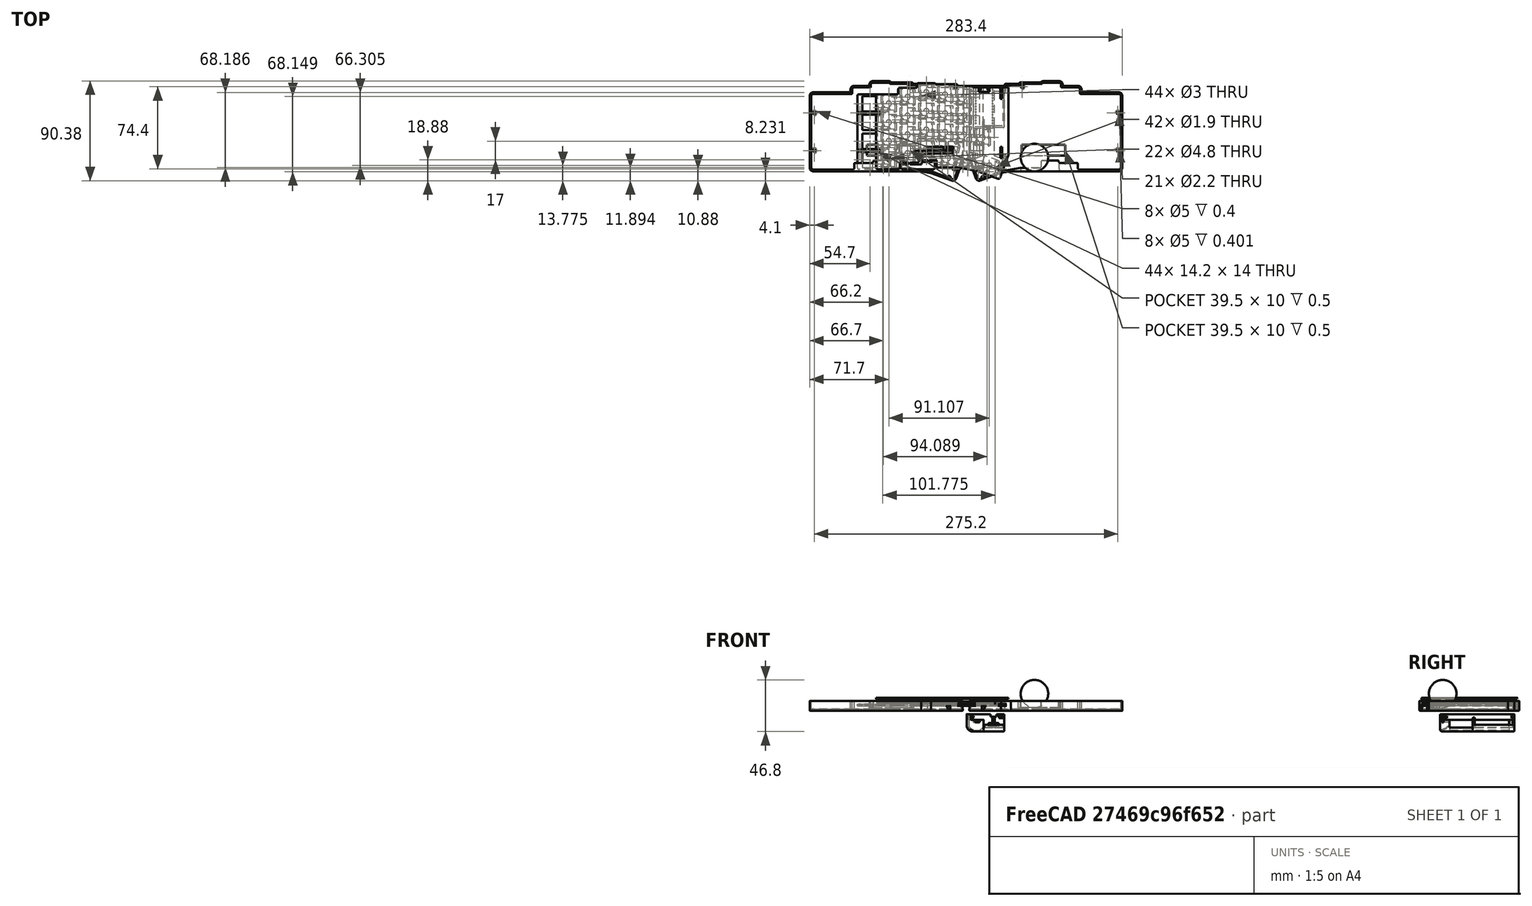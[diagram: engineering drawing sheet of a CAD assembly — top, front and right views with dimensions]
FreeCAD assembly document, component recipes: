
FREECAD ASSEMBLY — COMPONENT RECIPES ("simple-case-MS")

This assembly document has 5 components, labeled P0..P4 below (a component is one placed body or linked part). 4 of them carry a construction recipe — the FreeCAD feature program that regenerates the part from scratch, quoted from this document or its linked companion documents; the rest are supplied as boundary geometry only. No exploded tour is included for this assembly.
NOTE — document 3 of 3 of this assembly tour. The two overview renders and the header above are repeated from document 1; the component sections below continue where the previous document stopped.
COMPONENT P3 — recipe-attached ("case-trackball001", modeled in this document).
Construction recipe (the document's own serialized feature program — sketch geometry with constraints, then the solid features built on it; lengths are millimeters unless a unit is written):

FEATURE [Sketcher::SketchObject] Sketch028  label="top-plate001"
  ArcFitTolerance = 1e-06
  ExternalTypes = [0]
  FullyConstrained = true
  MakeInternals = false
  Placement = pos=(0,0,6.6e-15) rot=(0,0,1;0rad)
  _ExternalGeoVersion = 0
  sketch-geometry (128):
    g0: ArcOfCircle CenterX=45.3 CenterY=2.4 CenterZ=0 NormalX=-1e-16 NormalY=0 NormalZ=1 AngleXU=1.5708 Radius=1.5 StartAngle=0 EndAngle=1.22777
    g1: LineSegment StartX=59.4 StartY=3.9 StartZ=0 EndX=45.3 EndY=3.9 EndZ=0
    g2: LineSegment StartX=43.8874 StartY=2.9045 StartZ=0 EndX=43.8874 EndY=2.8 EndZ=0
    g3: ArcOfCircle CenterX=59.4 CenterY=2.4 CenterZ=0 NormalX=-1e-16 NormalY=0 NormalZ=1 AngleXU=3.90995e-07 Radius=1.5 StartAngle=0 EndAngle=1.5708
    g4: LineSegment StartX=60.9 StartY=-0.4 StartZ=0 EndX=60.9 EndY=2.4 EndZ=0
    g5: LineSegment StartX=76.4 StartY=-0.4 StartZ=0 EndX=60.9 EndY=-0.4 EndZ=0
    g6: ArcOfCircle CenterX=76.4 CenterY=-1.9 CenterZ=0 NormalX=-1e-16 NormalY=0 NormalZ=1 AngleXU=3.90995e-07 Radius=1.5 StartAngle=0 EndAngle=1.5708
    g7: LineSegment StartX=77.9 StartY=-6.3 StartZ=0 EndX=77.9 EndY=-1.9 EndZ=0
    g8: LineSegment StartX=96.4 StartY=-6.3 StartZ=0 EndX=77.9 EndY=-6.3 EndZ=0
    g9: ArcOfCircle CenterX=96.4 CenterY=-7.8 CenterZ=0 NormalX=-1e-16 NormalY=0 NormalZ=1 AngleXU=3.90995e-07 Radius=1.5 StartAngle=0 EndAngle=1.5708
    g10: LineSegment StartX=97.9 StartY=-59.8 StartZ=0 EndX=97.9 EndY=-7.8 EndZ=0
    g11: LineSegment StartX=97.9 StartY=-72.8 StartZ=0 EndX=97.9 EndY=-59.8 EndZ=0
    g12: ArcOfCircle CenterX=96.4 CenterY=-72.8 CenterZ=0 NormalX=-1e-16 NormalY=0 NormalZ=1 AngleXU=-1.5708 Radius=1.5 StartAngle=0 EndAngle=1.5708
    g13: LineSegment StartX=78 StartY=-74.3 StartZ=0 EndX=96.4 EndY=-74.3 EndZ=0
    g14: ArcOfCircle CenterX=78 CenterY=-72.8 CenterZ=0 NormalX=-1e-16 NormalY=0 NormalZ=1 AngleXU=-3.14159 Radius=1.5 StartAngle=0 EndAngle=1.5708
    g15: LineSegment StartX=76.5 StartY=-68.4 StartZ=0 EndX=76.5 EndY=-72.8 EndZ=0
    g16: LineSegment StartX=60.7 StartY=-68.4 StartZ=0 EndX=76.5 EndY=-68.4 EndZ=0
    g17: ArcOfCircle CenterX=60.7 CenterY=-66.9 CenterZ=0 NormalX=-1e-16 NormalY=0 NormalZ=1 AngleXU=-3.14159 Radius=1.5 StartAngle=0 EndAngle=1.5708
    g18: LineSegment StartX=59.2 StartY=-66.1 StartZ=0 EndX=59.2 EndY=-66.9 EndZ=0
    g19: LineSegment StartX=43.1 StartY=-66.1 StartZ=0 EndX=59.2 EndY=-66.1 EndZ=0
    g20: LineSegment StartX=43.1 StartY=-71.2 StartZ=0 EndX=43.1 EndY=-66.1 EndZ=0
    g21: ArcOfCircle CenterX=41.6 CenterY=-71.2 CenterZ=0 NormalX=-1e-16 NormalY=0 NormalZ=1 AngleXU=-1.5708 Radius=1.5 StartAngle=0 EndAngle=1.5708
    g22: LineSegment StartX=41.4 StartY=-72.7 StartZ=0 EndX=41.6 EndY=-72.7 EndZ=0
    g23: LineSegment StartX=24.227 StartY=-72.7043 StartZ=0 EndX=41.4 EndY=-72.7 EndZ=0
    g24: LineSegment StartX=6.18739 StartY=-75.9853 StartZ=0 EndX=24.227 EndY=-72.7043 EndZ=0
    g25: LineSegment StartX=-12.4977 StartY=-82.7894 StartZ=0 EndX=6.18739 EndY=-75.9853 EndZ=0
    g26: ArcOfCircle CenterX=-13.0109 CenterY=-81.3798 CenterZ=0 NormalX=-1e-16 NormalY=0 NormalZ=1 AngleXU=-2.78723 Radius=1.50005 StartAngle=0 EndAngle=1.56562
    g27: LineSegment StartX=-20.3 StartY=-66 StartZ=0 EndX=-14.4178 EndY=-81.9004 EndZ=0
    g28: LineSegment StartX=-9.1 StartY=-61.9235 StartZ=0 EndX=-20.3 EndY=-66 EndZ=0
    g29: LineSegment StartX=-9.1 StartY=-61 StartZ=0 EndX=-9.1 EndY=-61.9235 EndZ=0
    g30: LineSegment StartX=-9.1 StartY=-36.9 StartZ=0 EndX=-9.1 EndY=-61 EndZ=0
    g31: LineSegment StartX=9.9 StartY=-36.9 StartZ=0 EndX=-9.1 EndY=-36.9 EndZ=0
    g32: LineSegment StartX=9.9 StartY=1.3 StartZ=0 EndX=9.9 EndY=-36.9 EndZ=0
    g33: LineSegment StartX=23.7 StartY=1.3 StartZ=0 EndX=9.9 EndY=1.3 EndZ=0
    g34: ArcOfCircle CenterX=25.2 CenterY=1.3 CenterZ=0 NormalX=-1e-16 NormalY=0 NormalZ=1 AngleXU=1.5708 Radius=1.5 StartAngle=0 EndAngle=1.5708
    g35: LineSegment StartX=43.8874 StartY=2.8 StartZ=0 EndX=25.2 EndY=2.8 EndZ=0
    g36: LineSegment StartX=93.5 StartY=-72.8 StartZ=0 EndX=79.3 EndY=-72.8 EndZ=0
    g37: LineSegment StartX=93.5 StartY=-58.8 StartZ=0 EndX=93.5 EndY=-72.8 EndZ=0
    g38: LineSegment StartX=79.3 StartY=-58.8 StartZ=0 EndX=93.5 EndY=-58.8 EndZ=0
    g39: LineSegment StartX=79.3 StartY=-72.8 StartZ=0 EndX=79.3 EndY=-58.8 EndZ=0
    g40: LineSegment StartX=76.5 StartY=-66.85 StartZ=0 EndX=62.3 EndY=-66.85 EndZ=0
    g41: LineSegment StartX=76.5 StartY=-52.85 StartZ=0 EndX=76.5 EndY=-66.85 EndZ=0
    g42: LineSegment StartX=62.3 StartY=-52.85 StartZ=0 EndX=76.5 EndY=-52.85 EndZ=0
    g43: LineSegment StartX=62.3 StartY=-66.85 StartZ=0 EndX=62.3 EndY=-52.85 EndZ=0
    g44: Circle CenterX=95.6 CenterY=-57.3 CenterZ=0 NormalX=-1e-16 NormalY=0 NormalZ=1 AngleXU=-1.5708 Radius=1.1
    g45: LineSegment StartX=93.5 StartY=-55.8 StartZ=0 EndX=79.3 EndY=-55.8 EndZ=0
    g46: LineSegment StartX=93.5 StartY=-41.8 StartZ=0 EndX=93.5 EndY=-55.8 EndZ=0
    g47: LineSegment StartX=79.3 StartY=-41.8 StartZ=0 EndX=93.5 EndY=-41.8 EndZ=0
    g48: LineSegment StartX=79.3 StartY=-55.8 StartZ=0 EndX=79.3 EndY=-41.8 EndZ=0
    g49: LineSegment StartX=76.5 StartY=-49.85 StartZ=0 EndX=62.3 EndY=-49.85 EndZ=0
    g50: LineSegment StartX=76.5 StartY=-35.85 StartZ=0 EndX=76.5 EndY=-49.85 EndZ=0
    g51: LineSegment StartX=62.3 StartY=-35.85 StartZ=0 EndX=76.5 EndY=-35.85 EndZ=0
    g52: LineSegment StartX=62.3 StartY=-49.85 StartZ=0 EndX=62.3 EndY=-35.85 EndZ=0
    g53: LineSegment StartX=59.5 StartY=-62.6 StartZ=0 EndX=45.3 EndY=-62.6 EndZ=0
    g54: LineSegment StartX=59.5 StartY=-48.6 StartZ=0 EndX=59.5 EndY=-62.6 EndZ=0
    g55: LineSegment StartX=45.3 StartY=-48.6 StartZ=0 EndX=59.5 EndY=-48.6 EndZ=0
    g56: LineSegment StartX=45.3 StartY=-62.6 StartZ=0 EndX=45.3 EndY=-48.6 EndZ=0
    g57: LineSegment StartX=39.95 StartY=-71.1 StartZ=0 EndX=25.75 EndY=-71.1 EndZ=0
    g58: LineSegment StartX=39.95 StartY=-57.1 StartZ=0 EndX=39.95 EndY=-71.1 EndZ=0
    g59: LineSegment StartX=25.75 StartY=-57.1 StartZ=0 EndX=39.95 EndY=-57.1 EndZ=0
    g60: LineSegment StartX=25.75 StartY=-71.1 StartZ=0 EndX=25.75 EndY=-57.1 EndZ=0
    g61: LineSegment StartX=21.8608 StartY=-71.3659 StartZ=0 EndX=7.87653 EndY=-73.8317 EndZ=0
    g62: LineSegment StartX=19.4297 StartY=-57.5786 StartZ=0 EndX=21.8608 EndY=-71.3659 EndZ=0
    g63: LineSegment StartX=5.44545 StartY=-60.0444 StartZ=0 EndX=19.4297 EndY=-57.5786 EndZ=0
    g64: LineSegment StartX=7.87653 StartY=-73.8317 StartZ=0 EndX=5.44545 EndY=-60.0444 EndZ=0
    g65: LineSegment StartX=4.35879 StartY=-75.0546 StartZ=0 EndX=-8.98485 EndY=-79.9113 EndZ=0
    g66: LineSegment StartX=-0.429495 StartY=-61.8989 StartZ=0 EndX=4.35879 EndY=-75.0546 EndZ=0
    g67: LineSegment StartX=-13.7731 StartY=-66.7556 StartZ=0 EndX=-0.429495 EndY=-61.8989 EndZ=0
    g68: LineSegment StartX=-8.98485 StartY=-79.9113 StartZ=0 EndX=-13.7731 EndY=-66.7556 EndZ=0
    g69: Circle CenterX=-14 CenterY=-73.8 CenterZ=0 NormalX=-1e-16 NormalY=0 NormalZ=1 AngleXU=-1.5708 Radius=1.1
    g70: LineSegment StartX=42.5 StartY=-47.725 StartZ=0 EndX=28.3 EndY=-47.725 EndZ=0
    g71: LineSegment StartX=42.5 StartY=-33.725 StartZ=0 EndX=42.5 EndY=-47.725 EndZ=0
    g72: LineSegment StartX=28.3 StartY=-33.725 StartZ=0 EndX=42.5 EndY=-33.725 EndZ=0
    g73: LineSegment StartX=28.3 StartY=-47.725 StartZ=0 EndX=28.3 EndY=-33.725 EndZ=0
    g74: LineSegment StartX=25.5 StartY=-49.85 StartZ=0 EndX=11.3 EndY=-49.85 EndZ=0
    g75: LineSegment StartX=25.5 StartY=-35.85 StartZ=0 EndX=25.5 EndY=-49.85 EndZ=0
    g76: LineSegment StartX=11.3 StartY=-35.85 StartZ=0 EndX=25.5 EndY=-35.85 EndZ=0
    g77: LineSegment StartX=11.3 StartY=-49.85 StartZ=0 EndX=11.3 EndY=-35.85 EndZ=0
    g78: LineSegment StartX=8.5 StartY=-52.4 StartZ=0 EndX=-5.7 EndY=-52.4 EndZ=0
    g79: LineSegment StartX=8.5 StartY=-38.4 StartZ=0 EndX=8.5 EndY=-52.4 EndZ=0
    g80: LineSegment StartX=-5.7 StartY=-38.4 StartZ=0 EndX=8.5 EndY=-38.4 EndZ=0
    g81: LineSegment StartX=-5.7 StartY=-52.4 StartZ=0 EndX=-5.7 EndY=-38.4 EndZ=0
    g82: LineSegment StartX=93.5 StartY=-38.8 StartZ=0 EndX=79.3 EndY=-38.8 EndZ=0
    g83: LineSegment StartX=93.5 StartY=-24.8 StartZ=0 EndX=93.5 EndY=-38.8 EndZ=0
    g84: LineSegment StartX=79.3 StartY=-24.8 StartZ=0 EndX=93.5 EndY=-24.8 EndZ=0
    g85: LineSegment StartX=79.3 StartY=-38.8 StartZ=0 EndX=79.3 EndY=-24.8 EndZ=0
    g86: Circle CenterX=95.6 CenterY=-23.3 CenterZ=0 NormalX=-1e-16 NormalY=0 NormalZ=1 AngleXU=-1.5708 Radius=1.1
    g87: LineSegment StartX=76.5 StartY=-32.85 StartZ=0 EndX=62.3 EndY=-32.85 EndZ=0
    g88: LineSegment StartX=76.5 StartY=-18.85 StartZ=0 EndX=76.5 EndY=-32.85 EndZ=0
    g89: LineSegment StartX=62.3 StartY=-18.85 StartZ=0 EndX=76.5 EndY=-18.85 EndZ=0
    g90: LineSegment StartX=62.3 StartY=-32.85 StartZ=0 EndX=62.3 EndY=-18.85 EndZ=0
    g91: LineSegment StartX=59.5 StartY=-45.6 StartZ=0 EndX=45.3 EndY=-45.6 EndZ=0
    g92: LineSegment StartX=59.5 StartY=-31.6 StartZ=0 EndX=59.5 EndY=-45.6 EndZ=0
    g93: LineSegment StartX=45.3 StartY=-31.6 StartZ=0 EndX=59.5 EndY=-31.6 EndZ=0
    g94: LineSegment StartX=45.3 StartY=-45.6 StartZ=0 EndX=45.3 EndY=-31.6 EndZ=0
    g95: LineSegment StartX=59.5 StartY=-28.6 StartZ=0 EndX=45.3 EndY=-28.6 EndZ=0
    g96: LineSegment StartX=59.5 StartY=-14.6 StartZ=0 EndX=59.5 EndY=-28.6 EndZ=0
    g97: LineSegment StartX=45.3 StartY=-14.6 StartZ=0 EndX=59.5 EndY=-14.6 EndZ=0
    g98: LineSegment StartX=45.3 StartY=-28.6 StartZ=0 EndX=45.3 EndY=-14.6 EndZ=0
    g99: LineSegment StartX=93.5 StartY=-21.8 StartZ=0 EndX=79.3 EndY=-21.8 EndZ=0
    g100: LineSegment StartX=93.5 StartY=-7.8 StartZ=0 EndX=93.5 EndY=-21.8 EndZ=0
    g101: LineSegment StartX=79.3 StartY=-7.8 StartZ=0 EndX=93.5 EndY=-7.8 EndZ=0
    g102: LineSegment StartX=79.3 StartY=-21.8 StartZ=0 EndX=79.3 EndY=-7.8 EndZ=0
    g103: LineSegment StartX=76.5 StartY=-15.85 StartZ=0 EndX=62.3 EndY=-15.85 EndZ=0
    g104: LineSegment StartX=76.5 StartY=-1.85 StartZ=0 EndX=76.5 EndY=-15.85 EndZ=0
    g105: LineSegment StartX=62.3 StartY=-1.85 StartZ=0 EndX=76.5 EndY=-1.85 EndZ=0
    g106: LineSegment StartX=62.3 StartY=-15.85 StartZ=0 EndX=62.3 EndY=-1.85 EndZ=0
    g107: LineSegment StartX=59.5 StartY=-11.6 StartZ=0 EndX=45.3 EndY=-11.6 EndZ=0
    g108: LineSegment StartX=59.5 StartY=2.4 StartZ=0 EndX=59.5 EndY=-11.6 EndZ=0
    g109: LineSegment StartX=45.3 StartY=2.4 StartZ=0 EndX=59.5 EndY=2.4 EndZ=0
    g110: LineSegment StartX=45.3 StartY=-11.6 StartZ=0 EndX=45.3 EndY=2.4 EndZ=0
    g111: LineSegment StartX=42.5 StartY=-30.725 StartZ=0 EndX=28.3 EndY=-30.725 EndZ=0
    g112: LineSegment StartX=42.5 StartY=-16.725 StartZ=0 EndX=42.5 EndY=-30.725 EndZ=0
    g113: LineSegment StartX=28.3 StartY=-16.725 StartZ=0 EndX=42.5 EndY=-16.725 EndZ=0
    g114: LineSegment StartX=28.3 StartY=-30.725 StartZ=0 EndX=28.3 EndY=-16.725 EndZ=0
    g115: LineSegment StartX=25.5 StartY=-32.85 StartZ=0 EndX=11.3 EndY=-32.85 EndZ=0
    g116: LineSegment StartX=25.5 StartY=-18.85 StartZ=0 EndX=25.5 EndY=-32.85 EndZ=0
    g117: LineSegment StartX=11.3 StartY=-18.85 StartZ=0 EndX=25.5 EndY=-18.85 EndZ=0
    g118: LineSegment StartX=11.3 StartY=-32.85 StartZ=0 EndX=11.3 EndY=-18.85 EndZ=0
    g119: LineSegment StartX=25.5 StartY=-15.85 StartZ=0 EndX=11.3 EndY=-15.85 EndZ=0
    g120: LineSegment StartX=25.5 StartY=-1.85 StartZ=0 EndX=25.5 EndY=-15.85 EndZ=0
    g121: LineSegment StartX=11.3 StartY=-1.85 StartZ=0 EndX=25.5 EndY=-1.85 EndZ=0
    g122: LineSegment StartX=11.3 StartY=-15.85 StartZ=0 EndX=11.3 EndY=-1.85 EndZ=0
    g123: LineSegment StartX=42.5 StartY=-13.725 StartZ=0 EndX=28.3 EndY=-13.725 EndZ=0
    g124: LineSegment StartX=42.5 StartY=0.275 StartZ=0 EndX=42.5 EndY=-13.725 EndZ=0
    g125: LineSegment StartX=28.3 StartY=0.275 StartZ=0 EndX=42.5 EndY=0.275 EndZ=0
    g126: LineSegment StartX=28.3 StartY=-13.725 StartZ=0 EndX=28.3 EndY=0.275 EndZ=0
    g127: Circle CenterX=25.9 CenterY=0.6 CenterZ=0 NormalX=-1e-16 NormalY=0 NormalZ=1 AngleXU=-1.5708 Radius=1.1
  constraints (252):
    c: Block(g0)
    c: Block(g1)
    c: Block(g2)
    c: Block(g3)
    c: Block(g4)
    c: Block(g5)
    c: Block(g6)
    c: Block(g7)
    c: Block(g8)
    c: Block(g9)
    c: Block(g10)
    c: Block(g11)
    c: Block(g12)
    c: Block(g13)
    c: Block(g14)
    c: Block(g15)
    c: Block(g16)
    c: Block(g17)
    c: Block(g18)
    c: Block(g19)
    c: Block(g20)
    c: Block(g21)
    c: Block(g22)
    c: Block(g23)
    c: Block(g24)
    c: Block(g25)
    c: Block(g26)
    c: Block(g27)
    c: Block(g28)
    c: Block(g29)
    c: Block(g30)
    c: Block(g31)
    c: Block(g32)
    c: Block(g33)
    c: Block(g34)
    c: Block(g35)
    c: Block(g36)
    c: Block(g37)
    c: Block(g38)
    c: Block(g39)
    c: Block(g40)
    c: Block(g41)
    c: Block(g42)
    c: Block(g43)
    c: Block(g44)
    c: Block(g45)
    c: Block(g46)
    c: Block(g47)
    c: Block(g48)
    c: Block(g49)
    c: Block(g50)
    c: Block(g51)
    c: Block(g52)
    c: Block(g53)
    c: Block(g54)
    c: Block(g55)
    c: Block(g56)
    c: Block(g57)
    c: Block(g58)
    c: Block(g59)
    c: Block(g60)
    c: Block(g61)
    c: Block(g62)
    c: Block(g63)
    c: Block(g64)
    c: Block(g65)
    c: Block(g66)
    c: Block(g67)
    c: Block(g68)
    c: Block(g69)
    c: Block(g70)
    c: Block(g71)
    c: Block(g72)
    c: Block(g73)
    c: Block(g74)
    c: Block(g75)
    c: Block(g76)
    c: Block(g77)
    c: Block(g78)
    c: Block(g79)
    c: Block(g80)
    c: Block(g81)
    c: Block(g82)
    c: Block(g83)
    c: Block(g84)
    c: Block(g85)
    c: Block(g86)
    c: Block(g87)
    c: Block(g88)
    c: Block(g89)
    c: Block(g90)
    c: Block(g91)
    c: Block(g92)
    c: Block(g93)
    c: Block(g94)
    c: Block(g95)
    c: Block(g96)
    c: Block(g97)
    c: Block(g98)
    c: Block(g99)
    c: Block(g100)
    c: Block(g101)
    c: Block(g102)
    c: Block(g103)
    c: Block(g104)
    c: Block(g105)
    c: Block(g106)
    c: Block(g107)
    c: Block(g108)
    c: Block(g109)
    c: Block(g110)
    c: Block(g111)
    c: Block(g112)
    c: Block(g113)
    c: Block(g114)
    c: Block(g115)
    c: Block(g116)
    c: Block(g117)
    c: Block(g118)
    c: Block(g119)
    c: Block(g120)
    c: Block(g121)
    c: Block(g122)
    c: Block(g123)
    c: Block(g124)
    c: Block(g125)
    c: Block(g126)
    c: Block(g127)
    c: Coincident(g27,g28)
    c: Coincident(g26,g27)
    c: Coincident(g67,g68)
    c: Coincident(g25,g26)
    c: Coincident(g28,g29)
    c: Coincident(g29,g30)
    c: Coincident(g30,g31)
    c: Coincident(g65,g68)
    c: Coincident(g78,g81)
    c: Coincident(g80,g81)
    c: Coincident(g66,g67)
    c: Coincident(g65,g66)
    c: Coincident(g63,g64)
    c: Coincident(g24,g25)
    c: Coincident(g61,g64)
    c: Coincident(g78,g79)
    c: Coincident(g79,g80)
    c: Coincident(g31,g32)
    c: Coincident(g32,g33)
    c: Coincident(g74,g77)
    c: Coincident(g76,g77)
    c: Coincident(g115,g118)
    c: Coincident(g117,g118)
    c: Coincident(g119,g122)
    c: Coincident(g121,g122)
    c: Coincident(g62,g63)
    c: Coincident(g61,g62)
    c: Coincident(g33,g34)
    c: Coincident(g23,g24)
    c: Coincident(g34,g35)
    c: Coincident(g74,g75)
    c: Coincident(g75,g76)
    c: Coincident(g115,g116)
    c: Coincident(g116,g117)
    c: Coincident(g119,g120)
    c: Coincident(g120,g121)
    c: Coincident(g57,g60)
    c: Coincident(g59,g60)
    c: Coincident(g70,g73)
    c: Coincident(g72,g73)
    c: Coincident(g111,g114)
    c: Coincident(g113,g114)
    c: Coincident(g123,g126)
    c: Coincident(g125,g126)
    c: Coincident(g57,g58)
    c: Coincident(g58,g59)
    c: Coincident(g22,g23)
    c: Coincident(g21,g22)
    c: Coincident(g70,g71)
    c: Coincident(g71,g72)
    c: Coincident(g111,g112)
    c: Coincident(g112,g113)
    c: Coincident(g123,g124)
    c: Coincident(g124,g125)
    c: Coincident(g20,g21)
    c: Coincident(g19,g20)
    c: Coincident(g2,g35)
    c: Coincident(g0,g2)
    c: Coincident(g53,g56)
    c: Coincident(g55,g56)
    c: Coincident(g91,g94)
    c: Coincident(g93,g94)
    c: Coincident(g95,g98)
    c: Coincident(g97,g98)
    c: Coincident(g107,g110)
    c: Coincident(g109,g110)
    c: Coincident(g0,g1)
    c: Coincident(g17,g18)
    c: Coincident(g18,g19)
    c: Coincident(g1,g3)
    c: Coincident(g53,g54)
    c: Coincident(g54,g55)
    c: Coincident(g91,g92)
    c: Coincident(g92,g93)
    c: Coincident(g95,g96)
    c: Coincident(g96,g97)
    c: Coincident(g107,g108)
    c: Coincident(g108,g109)
    c: Coincident(g16,g17)
    c: Coincident(g4,g5)
    c: Coincident(g3,g4)
    c: Coincident(g40,g43)
    c: Coincident(g42,g43)
    c: Coincident(g49,g52)
    c: Coincident(g51,g52)
    c: Coincident(g87,g90)
    c: Coincident(g89,g90)
    c: Coincident(g103,g106)
    c: Coincident(g105,g106)
    c: Coincident(g5,g6)
    c: Coincident(g14,g15)
    c: Coincident(g15,g16)
    c: Coincident(g40,g41)
    c: Coincident(g41,g42)
    c: Coincident(g49,g50)
    c: Coincident(g50,g51)
    c: Coincident(g87,g88)
    c: Coincident(g88,g89)
    c: Coincident(g103,g104)
    c: Coincident(g104,g105)
    c: Coincident(g7,g8)
    c: Coincident(g6,g7)
    c: Coincident(g13,g14)
    c: Coincident(g36,g39)
    c: Coincident(g38,g39)
    c: Coincident(g45,g48)
    c: Coincident(g47,g48)
    c: Coincident(g82,g85)
    c: Coincident(g84,g85)
    c: Coincident(g99,g102)
    c: Coincident(g101,g102)
    c: Coincident(g36,g37)
    c: Coincident(g37,g38)
    c: Coincident(g45,g46)
    c: Coincident(g46,g47)
    c: Coincident(g82,g83)
    c: Coincident(g83,g84)
    c: Coincident(g99,g100)
    c: Coincident(g100,g101)
    c: Coincident(g12,g13)
    c: Coincident(g8,g9)
    c: Coincident(g11,g12)
    c: Coincident(g10,g11)
    c: Coincident(g9,g10)
FEATURE [Sketcher::SketchObject] Sketch029
  ArcFitTolerance = 1e-06
  AttachmentOffset = pos=(0,0,-5.1) rot=(0,0,1;0rad)
  AttachmentSupport = -> [XY_Plane005]
  ExternalTypes = [0]
  FullyConstrained = false
  MakeInternals = false
  MapMode = 5
  Placement = pos=(0,0,-5.1) rot=(0,0,1;0rad)
  _ExternalGeoVersion = 0
  sketch-geometry (65):
    g0: ArcOfCircle [constr] CenterX=45.3 CenterY=2.4 CenterZ=0 NormalX=-1e-16 NormalY=0 NormalZ=1 AngleXU=1.5708 Radius=1.5 StartAngle=0 EndAngle=1.22777
    g1: LineSegment [constr] StartX=59.4 StartY=3.9 StartZ=0 EndX=45.3 EndY=3.9 EndZ=0
    g2: LineSegment [constr] StartX=43.8874 StartY=2.9045 StartZ=0 EndX=43.8874 EndY=2.8 EndZ=0
    g3: ArcOfCircle [constr] CenterX=59.4 CenterY=2.4 CenterZ=0 NormalX=-1e-16 NormalY=0 NormalZ=1 AngleXU=3.90995e-07 Radius=1.5 StartAngle=0 EndAngle=1.5708
    g4: LineSegment [constr] StartX=60.9 StartY=-0.4 StartZ=0 EndX=60.9 EndY=2.4 EndZ=0
    g5: LineSegment [constr] StartX=76.4 StartY=-0.4 StartZ=0 EndX=60.9 EndY=-0.4 EndZ=0
    g6: ArcOfCircle [constr] CenterX=76.4 CenterY=-1.9 CenterZ=0 NormalX=-1e-16 NormalY=0 NormalZ=1 AngleXU=3.90995e-07 Radius=1.5 StartAngle=0 EndAngle=1.5708
    g7: LineSegment [constr] StartX=77.9 StartY=-6.3 StartZ=0 EndX=77.9 EndY=-1.9 EndZ=0
    g8: LineSegment [constr] StartX=96.4 StartY=-6.3 StartZ=0 EndX=77.9 EndY=-6.3 EndZ=0
    g9: ArcOfCircle [constr] CenterX=96.4 CenterY=-7.8 CenterZ=0 NormalX=-1e-16 NormalY=0 NormalZ=1 AngleXU=3.90995e-07 Radius=1.5 StartAngle=0 EndAngle=1.5708
    g10: LineSegment [constr] StartX=97.9 StartY=-59.8 StartZ=0 EndX=97.9 EndY=-7.8 EndZ=0
    g11: LineSegment [constr] StartX=97.9 StartY=-72.8 StartZ=0 EndX=97.9 EndY=-59.8 EndZ=0
    g12: ArcOfCircle [constr] CenterX=96.4 CenterY=-72.8 CenterZ=0 NormalX=-1e-16 NormalY=0 NormalZ=1 AngleXU=-1.5708 Radius=1.5 StartAngle=0 EndAngle=1.5708
    g13: LineSegment [constr] StartX=78 StartY=-74.3 StartZ=0 EndX=96.4 EndY=-74.3 EndZ=0
    g14: LineSegment [constr] StartX=6.18739 StartY=-75.9853 StartZ=0 EndX=15.4535 EndY=-74.3 EndZ=0
    g15: LineSegment [constr] StartX=-12.4977 StartY=-82.7894 StartZ=0 EndX=6.18739 EndY=-75.9853 EndZ=0
    g16: ArcOfCircle [constr] CenterX=-13.0109 CenterY=-81.3798 CenterZ=0 NormalX=-1e-16 NormalY=0 NormalZ=1 AngleXU=-2.78723 Radius=1.50005 StartAngle=0 EndAngle=1.56562
    g17: LineSegment [constr] StartX=-20.3 StartY=-66 StartZ=0 EndX=-14.4178 EndY=-81.9004 EndZ=0
    g18: LineSegment [constr] StartX=-9.1 StartY=-61.9235 StartZ=0 EndX=-20.3 EndY=-66 EndZ=0
    g19: LineSegment [constr] StartX=-9.1 StartY=-61 StartZ=0 EndX=-9.1 EndY=-61.9235 EndZ=0
    g20: LineSegment [constr] StartX=-9.1 StartY=-36.9 StartZ=0 EndX=-9.1 EndY=-61 EndZ=0
    g21: LineSegment [constr] StartX=9.9 StartY=-36.9 StartZ=0 EndX=-9.1 EndY=-36.9 EndZ=0
    g22: LineSegment [constr] StartX=9.9 StartY=1.3 StartZ=0 EndX=9.9 EndY=-36.9 EndZ=0
    g23: LineSegment [constr] StartX=23.7 StartY=1.3 StartZ=0 EndX=9.9 EndY=1.3 EndZ=0
    g24: ArcOfCircle [constr] CenterX=25.2 CenterY=1.3 CenterZ=0 NormalX=-1e-16 NormalY=0 NormalZ=1 AngleXU=1.5708 Radius=1.5 StartAngle=0 EndAngle=1.5708
    g25: LineSegment [constr] StartX=43.8874 StartY=2.8 StartZ=0 EndX=25.2 EndY=2.8 EndZ=0
    g26: LineSegment [constr] StartX=78 StartY=-74.3 StartZ=0 EndX=15.4535 EndY=-74.3 EndZ=0
    g27: LineSegment StartX=78 StartY=-76.1 StartZ=0 EndX=15.6159 EndY=-76.1 EndZ=0
    g28: LineSegment StartX=6.65976 StartY=-77.7289 StartZ=0 EndX=15.6159 EndY=-76.1 EndZ=0
    g29: LineSegment StartX=-11.8818 StartY=-84.4807 StartZ=0 EndX=6.65976 EndY=-77.7289 EndZ=0
    g30: ArcOfCircle CenterX=-13.0109 CenterY=-81.3798 CenterZ=0 NormalX=0 NormalY=0 NormalZ=1 AngleXU=-2.78723 Radius=3.30007 StartAngle=6.28318 EndAngle=7.84881
    g31: LineSegment StartX=-21.9882 StartY=-66.6245 StartZ=0 EndX=-16.106 EndY=-82.5249 EndZ=0
    g32: LineSegment [constr] StartX=-10.9 StartY=-60.6632 StartZ=0 EndX=-20.9156 EndY=-64.3086 EndZ=0
    g33: LineSegment [constr] StartX=-10.9 StartY=-36.9 StartZ=0 EndX=-10.9 EndY=-60.6632 EndZ=0
    g34: ArcOfCircle [constr] CenterX=-9.1 CenterY=-36.9 CenterZ=0 NormalX=0 NormalY=0 NormalZ=1 AngleXU=0 Radius=1.8 StartAngle=1.5708 EndAngle=3.14159
    g35: LineSegment [constr] StartX=8.1 StartY=-35.1 StartZ=0 EndX=-9.1 EndY=-35.1 EndZ=0
    g36: LineSegment [constr] StartX=8.1 StartY=1.3 StartZ=0 EndX=8.1 EndY=-35.1 EndZ=0
    g37: ArcOfCircle [constr] CenterX=9.9 CenterY=1.3 CenterZ=0 NormalX=0 NormalY=0 NormalZ=1 AngleXU=0 Radius=1.8 StartAngle=1.5708 EndAngle=3.14159
    g38: LineSegment [constr] StartX=22.4341 StartY=3.1 StartZ=0 EndX=9.9 EndY=3.1 EndZ=0
    g39: ArcOfCircle CenterX=25.2 CenterY=1.3 CenterZ=0 NormalX=0 NormalY=0 NormalZ=1 AngleXU=1.5708 Radius=3.3 StartAngle=0 EndAngle=0.993864
    g40: LineSegment StartX=42.8403 StartY=4.6 StartZ=0 EndX=25.2 EndY=4.6 EndZ=0
    g41: ArcOfCircle CenterX=45.3 CenterY=2.4 CenterZ=0 NormalX=0 NormalY=0 NormalZ=1 AngleXU=1.5708 Radius=3.3 StartAngle=0 EndAngle=0.841069
    g42: LineSegment StartX=59.4 StartY=5.7 StartZ=0 EndX=45.3 EndY=5.7 EndZ=0
    g43: ArcOfCircle CenterX=59.4 CenterY=2.4 CenterZ=0 NormalX=0 NormalY=0 NormalZ=1 AngleXU=3.90995e-07 Radius=3.3 StartAngle=-1.8e-15 EndAngle=1.5708
    g44: LineSegment StartX=62.7 StartY=1.4 StartZ=0 EndX=62.7 EndY=2.4 EndZ=0
    g45: LineSegment StartX=76.4 StartY=1.4 StartZ=0 EndX=62.7 EndY=1.4 EndZ=0
    g46: ArcOfCircle CenterX=76.4 CenterY=-1.9 CenterZ=0 NormalX=0 NormalY=0 NormalZ=1 AngleXU=3.90995e-07 Radius=3.3 StartAngle=-1.8e-15 EndAngle=1.5708
    g47: LineSegment StartX=79.7 StartY=-4.5 StartZ=0 EndX=79.7 EndY=-1.9 EndZ=0
    g48: LineSegment StartX=113.4 StartY=-4.5 StartZ=0 EndX=79.7 EndY=-4.5 EndZ=0
    g49: ArcOfCircle CenterX=113.4 CenterY=-7.8 CenterZ=0 NormalX=0 NormalY=0 NormalZ=1 AngleXU=3.90995e-07 Radius=3.3 StartAngle=6.28318 EndAngle=7.85398
    g50: LineSegment StartX=116.7 StartY=-59.8 StartZ=0 EndX=116.7 EndY=-7.8 EndZ=0
    g51: LineSegment StartX=116.7 StartY=-72.8 StartZ=0 EndX=116.7 EndY=-59.8 EndZ=0
    g52: ArcOfCircle CenterX=113.4 CenterY=-72.8 CenterZ=0 NormalX=0 NormalY=0 NormalZ=1 AngleXU=-1.5708 Radius=3.3 StartAngle=6.80165e-06 EndAngle=1.5708
    g53: LineSegment StartX=78 StartY=-76.1 StartZ=0 EndX=113.4 EndY=-76.1 EndZ=0
    g54: LineSegment [constr] StartX=8.1 StartY=1.3 StartZ=0 EndX=8.1 EndY=0 EndZ=0
    g55: LineSegment StartX=8.1 StartY=0 StartZ=0 EndX=-22.1 EndY=0 EndZ=0
    g56: LineSegment StartX=-22.1 StartY=0 StartZ=0 EndX=-22.1 EndY=-61.0545 EndZ=0
    g57: LineSegment StartX=-22.1 StartY=-61.0545 StartZ=0 EndX=-20.3 EndY=-66 EndZ=0
    g58: LineSegment StartX=-20.3 StartY=-66 StartZ=0 EndX=-21.9882 EndY=-66.6245 EndZ=0
    g59: LineSegment StartX=22.4341 StartY=3.1 StartZ=0 EndX=8.1 EndY=3.1 EndZ=0
    g60: LineSegment StartX=8.1 StartY=3.1 StartZ=0 EndX=8.1 EndY=0 EndZ=0
    g61: LineSegment [constr] StartX=113.4 StartY=-7.8 StartZ=0 EndX=113.4 EndY=-4.5 EndZ=0
    g62: LineSegment [constr] StartX=113.4 StartY=-7.8 StartZ=0 EndX=116.7 EndY=-7.8 EndZ=0
    g63: LineSegment [constr] StartX=113.4 StartY=-72.8 StartZ=0 EndX=116.7 EndY=-72.8 EndZ=0
    g64: LineSegment [constr] StartX=113.4 StartY=-72.8 StartZ=0 EndX=113.4 EndY=-76.1 EndZ=0
  constraints (123):
    c: Block(g0)
    c: Block(g1)
    c: Block(g2)
    c: Block(g3)
    c: Block(g4)
    c: Block(g5)
    c: Block(g6)
    c: Block(g7)
    c: Block(g8)
    c: Block(g9)
    c: Block(g10)
    c: Block(g11)
    c: Block(g12)
    c: Block(g13)
    c: Block(g14)
    c: Block(g15)
    c: Block(g16)
    c: Block(g17)
    c: Block(g18)
    c: Block(g19)
    c: Block(g20)
    c: Block(g21)
    c: Block(g22)
    c: Block(g23)
    c: Block(g24)
    c: Block(g25)
    c: Coincident(g17,g18)
    c: Coincident(g16,g17)
    c: Coincident(g15,g16)
    c: Coincident(g18,g19)
    c: Coincident(g19,g20)
    c: Coincident(g20,g21)
    c: Coincident(g14,g15)
    c: Coincident(g21,g22)
    c: Coincident(g22,g23)
    c: Coincident(g23,g24)
    c: Coincident(g24,g25)
    c: Coincident(g2,g25)
    c: Coincident(g0,g2)
    c: Coincident(g0,g1)
    c: Coincident(g1,g3)
    c: Coincident(g4,g5)
    c: Coincident(g3,g4)
    c: Coincident(g5,g6)
    c: Coincident(g7,g8)
    c: Coincident(g6,g7)
    c: Coincident(g12,g13)
    c: Coincident(g8,g9)
    c: Coincident(g11,g12)
    c: Coincident(g10,g11)
    c: Coincident(g9,g10)
    c: Coincident(g26,g13)
    c: Horizontal(g26)
    c: Coincident(g14,g26)
    c: Coincident(g27,g28)
    c: Coincident(g27,g53)
    c: Coincident(g28,g29)
    c: Coincident(g32,g33)
    c: Tangent(g33,g34) = -1.5708
    c: Tangent(g34,g35) = -1.5708
    c: Coincident(g35,g36)
    c: Tangent(g36,g37) = -1.5708
    c: Tangent(g37,g38) = -1.5708
    c: Coincident(g38,g39)
    c: Coincident(g40,g41)
    c: Coincident(g44,g45)
    c: Coincident(g47,g48)
    c: Coincident(g50,g51)
    c: Coincident(g54,g36)
    c: PointOnObject(g54,g-1)
    c: Vertical(g54)
    c: Coincident(g55,g54)
    c: PointOnObject(g55,g-1)
    c: Coincident(g56,g55)
    c: Vertical(g56)
    c: DistanceX(g55,g-1) = 22.1
    c: Coincident(g57,g56)
    c: Coincident(g57,g17)
    c: Angle(g18,g57) = 1.5708
    c: Coincident(g58,g17)
    c: Coincident(g58,g31)
    c: Coincident(g30,g31)
    c: Coincident(g29,g30)
    c: Coincident(g39,g40)
    c: Coincident(g41,g42)
    c: Coincident(g42,g43)
    c: Coincident(g43,g44)
    c: Coincident(g45,g46)
    c: Coincident(g46,g47)
    c: Coincident(g52,g53)
    c: Coincident(g48,g49)
    c: Coincident(g51,g52)
    c: Coincident(g49,g50)
    c: Block(g38)
    c: Block(g36)
    c: Coincident(g59,g38)
    c: Horizontal(g59)
    c: Tangent(g59,g37)
    c: Coincident(g60,g59)
    c: Coincident(g60,g54)
    c: Vertical(g60)
    c: Block(g47)
    c: Block(g27)
    c: Radius(g49) = 3.3
    c: Radius(g52) = 3.3
    c: DistanceY(g51,g51) = 13
    c: DistanceY(g50,g50) = 52
    c: DistanceX(g48,g48) = 33.7
    c: Distance(g48,g-1) = 4.5
    c: DistanceY(g52,g-1) = 76.1
    c: Vertical(g51)
    c: Vertical(g50)
    c: Horizontal(g53)
    c: Coincident(g61,g49)
    c: Coincident(g61,g48)
    c: Vertical(g61)
    c: Coincident(g62,g49)
    c: Coincident(g62,g49)
    c: Horizontal(g62)
    c: Coincident(g63,g52)
    c: Coincident(g63,g51)
    c: Horizontal(g63)
    c: Vertical(g64)
FEATURE [PartDesign::Pad] Pad011
  Direction = (0,0,1)
  Length = 1.5
  Length2 = 7.3
  Profile = -> Sketch029
  ReferenceAxis = -> Sketch029 [N_Axis]
  Refine = true
  Reversed = true
  SideType = 1
  Suppressed = false
  Type = 0
  Type2 = 0
FEATURE [Sketcher::SketchObject] Sketch030  label="bottom-plate001"
  ArcFitTolerance = 1e-06
  ExternalTypes = [0]
  FullyConstrained = true
  MakeInternals = false
  Placement = pos=(0,0,6.6e-15) rot=(0,0,1;0rad)
  _ExternalGeoVersion = 0
  sketch-geometry (74):
    g0: ArcOfCircle CenterX=45.3 CenterY=2.4 CenterZ=0 NormalX=-1e-16 NormalY=0 NormalZ=1 AngleXU=1.5708 Radius=1.5 StartAngle=0 EndAngle=1.22777
    g1: LineSegment StartX=59.4 StartY=3.9 StartZ=0 EndX=45.3 EndY=3.9 EndZ=0
    g2: LineSegment StartX=43.8874 StartY=2.9045 StartZ=0 EndX=43.8874 EndY=2.8 EndZ=0
    g3: ArcOfCircle CenterX=59.4 CenterY=2.4 CenterZ=0 NormalX=-1e-16 NormalY=0 NormalZ=1 AngleXU=3.90995e-07 Radius=1.5 StartAngle=0 EndAngle=1.5708
    g4: LineSegment StartX=60.9 StartY=-0.4 StartZ=0 EndX=60.9 EndY=2.4 EndZ=0
    g5: LineSegment StartX=76.4 StartY=-0.4 StartZ=0 EndX=60.9 EndY=-0.4 EndZ=0
    g6: ArcOfCircle CenterX=76.4 CenterY=-1.9 CenterZ=0 NormalX=-1e-16 NormalY=0 NormalZ=1 AngleXU=3.90995e-07 Radius=1.5 StartAngle=0 EndAngle=1.5708
    g7: LineSegment StartX=77.9 StartY=-6.3 StartZ=0 EndX=77.9 EndY=-1.9 EndZ=0
    g8: LineSegment StartX=96.4 StartY=-6.3 StartZ=0 EndX=77.9 EndY=-6.3 EndZ=0
    g9: ArcOfCircle CenterX=96.4 CenterY=-7.8 CenterZ=0 NormalX=-1e-16 NormalY=0 NormalZ=1 AngleXU=3.90995e-07 Radius=1.5 StartAngle=0 EndAngle=1.5708
    g10: LineSegment StartX=97.9 StartY=-59.8 StartZ=0 EndX=97.9 EndY=-7.8 EndZ=0
    g11: LineSegment StartX=97.9 StartY=-72.8 StartZ=0 EndX=97.9 EndY=-59.8 EndZ=0
    g12: ArcOfCircle CenterX=96.4 CenterY=-72.8 CenterZ=0 NormalX=-1e-16 NormalY=0 NormalZ=1 AngleXU=-1.5708 Radius=1.5 StartAngle=0 EndAngle=1.5708
    g13: LineSegment StartX=78 StartY=-74.3 StartZ=0 EndX=96.4 EndY=-74.3 EndZ=0
    g14: ArcOfCircle CenterX=78 CenterY=-72.8 CenterZ=0 NormalX=-1e-16 NormalY=0 NormalZ=1 AngleXU=-3.14159 Radius=1.5 StartAngle=0 EndAngle=1.5708
    g15: LineSegment StartX=76.5 StartY=-68.4 StartZ=0 EndX=76.5 EndY=-72.8 EndZ=0
    g16: LineSegment StartX=68.6 StartY=-68.4 StartZ=0 EndX=76.5 EndY=-68.4 EndZ=0
    g17: LineSegment StartX=68.6 StartY=-69.9 StartZ=0 EndX=68.6 EndY=-68.4 EndZ=0
    g18: LineSegment StartX=75 StartY=-69.9 StartZ=0 EndX=68.6 EndY=-69.9 EndZ=0
    g19: LineSegment StartX=75 StartY=-72.8 StartZ=0 EndX=75 EndY=-69.9 EndZ=0
    g20: ArcOfCircle CenterX=73.5 CenterY=-72.8 CenterZ=0 NormalX=-1e-16 NormalY=0 NormalZ=1 AngleXU=-1.5708 Radius=1.5 StartAngle=0 EndAngle=1.5708
    g21: LineSegment StartX=46.1 StartY=-74.3 StartZ=0 EndX=73.5 EndY=-74.3 EndZ=0
    g22: ArcOfCircle CenterX=46.1 CenterY=-72.8 CenterZ=0 NormalX=-1e-16 NormalY=0 NormalZ=1 AngleXU=-3.14159 Radius=1.5 StartAngle=0 EndAngle=1.5708
    g23: LineSegment StartX=44.6 StartY=-67.6 StartZ=0 EndX=44.6 EndY=-72.8 EndZ=0
    g24: LineSegment StartX=49.65 StartY=-67.6 StartZ=0 EndX=44.6 EndY=-67.6 EndZ=0
    g25: LineSegment StartX=49.65 StartY=-66.1 StartZ=0 EndX=49.65 EndY=-67.6 EndZ=0
    g26: LineSegment StartX=43.1 StartY=-66.1 StartZ=0 EndX=49.65 EndY=-66.1 EndZ=0
    g27: LineSegment StartX=43.1 StartY=-71.2 StartZ=0 EndX=43.1 EndY=-66.1 EndZ=0
    g28: ArcOfCircle CenterX=41.6 CenterY=-71.2 CenterZ=0 NormalX=-1e-16 NormalY=0 NormalZ=1 AngleXU=-1.5708 Radius=1.5 StartAngle=0 EndAngle=1.5708
    g29: LineSegment StartX=41.4 StartY=-72.7 StartZ=0 EndX=41.6 EndY=-72.7 EndZ=0
    g30: LineSegment StartX=24.227 StartY=-72.7043 StartZ=0 EndX=41.4 EndY=-72.7 EndZ=0
    g31: LineSegment StartX=6.18739 StartY=-75.9853 StartZ=0 EndX=24.227 EndY=-72.7043 EndZ=0
    g32: LineSegment StartX=-12.4977 StartY=-82.7894 StartZ=0 EndX=6.18739 EndY=-75.9853 EndZ=0
    g33: ArcOfCircle CenterX=-13.011 CenterY=-81.3799 CenterZ=0 NormalX=-1e-16 NormalY=0 NormalZ=1 AngleXU=-2.78726 Radius=1.5 StartAngle=0 EndAngle=1.56568
    g34: LineSegment StartX=-22.1 StartY=-61.1344 StartZ=0 EndX=-14.4178 EndY=-81.9004 EndZ=0
    g35: LineSegment StartX=-22.1 StartY=0 StartZ=0 EndX=-22.1 EndY=-61.1344 EndZ=0
    g36: LineSegment StartX=-16.4 StartY=0 StartZ=0 EndX=-22.1 EndY=0 EndZ=0
    g37: LineSegment StartX=-16.4 StartY=-10.5 StartZ=0 EndX=-16.4 EndY=0 EndZ=0
    g38: LineSegment StartX=-14.8 StartY=-10.5 StartZ=0 EndX=-16.4 EndY=-10.5 EndZ=0
    g39: LineSegment StartX=-14.8 StartY=0 StartZ=0 EndX=-14.8 EndY=-10.5 EndZ=0
    g40: LineSegment StartX=-5 StartY=0 StartZ=0 EndX=-14.8 EndY=0 EndZ=0
    g41: LineSegment StartX=-5 StartY=-4 StartZ=0 EndX=-5 EndY=0 EndZ=0
    g42: LineSegment StartX=5 StartY=-4 StartZ=0 EndX=-5 EndY=-4 EndZ=0
    g43: LineSegment StartX=5 StartY=0 StartZ=0 EndX=5 EndY=-4 EndZ=0
    g44: LineSegment StartX=9.9 StartY=0 StartZ=0 EndX=5 EndY=0 EndZ=0
    g45: LineSegment StartX=9.9 StartY=1.3 StartZ=0 EndX=9.9 EndY=0 EndZ=0
    g46: LineSegment StartX=23.7 StartY=1.3 StartZ=0 EndX=9.9 EndY=1.3 EndZ=0
    g47: ArcOfCircle CenterX=25.2 CenterY=1.3 CenterZ=0 NormalX=-1e-16 NormalY=0 NormalZ=1 AngleXU=1.5708 Radius=1.5 StartAngle=0 EndAngle=1.5708
    g48: LineSegment StartX=43.8874 StartY=2.8 StartZ=0 EndX=25.2 EndY=2.8 EndZ=0
    g49: Circle CenterX=95.6 CenterY=-57.3 CenterZ=0 NormalX=-1e-16 NormalY=0 NormalZ=1 AngleXU=-1.5708 Radius=1.1
    g50: ArcOfCircle CenterX=60.7 CenterY=-66.9 CenterZ=0 NormalX=-1e-16 NormalY=0 NormalZ=1 AngleXU=-3.14159 Radius=1.5 StartAngle=0 EndAngle=1.5708
    g51: LineSegment StartX=59.2 StartY=-66.1 StartZ=0 EndX=59.2 EndY=-66.9 EndZ=0
    g52: LineSegment StartX=51.15 StartY=-66.1 StartZ=0 EndX=59.2 EndY=-66.1 EndZ=0
    g53: LineSegment StartX=51.15 StartY=-67.6 StartZ=0 EndX=51.15 EndY=-66.1 EndZ=0
    g54: LineSegment StartX=56.7 StartY=-67.6 StartZ=0 EndX=51.15 EndY=-67.6 EndZ=0
    g55: LineSegment StartX=56.7 StartY=-69.9 StartZ=0 EndX=56.7 EndY=-67.6 EndZ=0
    g56: LineSegment StartX=67.1 StartY=-69.9 StartZ=0 EndX=56.7 EndY=-69.9 EndZ=0
    g57: LineSegment StartX=67.1 StartY=-68.4 StartZ=0 EndX=67.1 EndY=-69.9 EndZ=0
    g58: LineSegment StartX=60.7 StartY=-68.4 StartZ=0 EndX=67.1 EndY=-68.4 EndZ=0
    g59: LineSegment StartX=62.7 StartY=-60 StartZ=0 EndX=27.8 EndY=-60 EndZ=0
    g60: LineSegment StartX=62.7 StartY=-57.6 StartZ=0 EndX=62.7 EndY=-60 EndZ=0
    g61: LineSegment StartX=27.8 StartY=-57.6 StartZ=0 EndX=62.7 EndY=-57.6 EndZ=0
    g62: LineSegment StartX=27.8 StartY=-60 StartZ=0 EndX=27.8 EndY=-57.6 EndZ=0
    g63: Circle CenterX=-14 CenterY=-73.8 CenterZ=0 NormalX=-1e-16 NormalY=0 NormalZ=1 AngleXU=-1.5708 Radius=1.1
    g64: LineSegment StartX=-14.8 StartY=-64.1 StartZ=0 EndX=-16.4 EndY=-64.1 EndZ=0
    g65: LineSegment StartX=-14.8 StartY=-54 StartZ=0 EndX=-14.8 EndY=-64.1 EndZ=0
    g66: LineSegment StartX=-16.4 StartY=-54 StartZ=0 EndX=-14.8 EndY=-54 EndZ=0
    g67: LineSegment StartX=-16.4 StartY=-64.1 StartZ=0 EndX=-16.4 EndY=-54 EndZ=0
    g68: LineSegment StartX=52 StartY=-56.2 StartZ=0 EndX=27.8 EndY=-56.2 EndZ=0
    g69: LineSegment StartX=52 StartY=-53.8 StartZ=0 EndX=52 EndY=-56.2 EndZ=0
    g70: LineSegment StartX=27.8 StartY=-53.8 StartZ=0 EndX=52 EndY=-53.8 EndZ=0
    g71: LineSegment StartX=27.8 StartY=-56.2 StartZ=0 EndX=27.8 EndY=-53.8 EndZ=0
    g72: Circle CenterX=95.6 CenterY=-23.3 CenterZ=0 NormalX=-1e-16 NormalY=0 NormalZ=1 AngleXU=-1.5708 Radius=1.1
    g73: Circle CenterX=25.9 CenterY=0.6 CenterZ=0 NormalX=-1e-16 NormalY=0 NormalZ=1 AngleXU=-1.5708 Radius=1.1
  constraints (144):
    c: Coincident(g34,g35)
    c: Coincident(g35,g36)
    c: Coincident(g64,g67)
    c: Coincident(g66,g67)
    c: Coincident(g37,g38)
    c: Coincident(g36,g37)
    c: Coincident(g64,g65)
    c: Coincident(g65,g66)
    c: Coincident(g38,g39)
    c: Coincident(g39,g40)
    c: Coincident(g33,g34)
    c: Coincident(g32,g33)
    c: Coincident(g41,g42)
    c: Coincident(g40,g41)
    c: Coincident(g42,g43)
    c: Coincident(g43,g44)
    c: Coincident(g31,g32)
    c: Coincident(g44,g45)
    c: Coincident(g45,g46)
    c: Coincident(g46,g47)
    c: Coincident(g30,g31)
    c: Coincident(g47,g48)
    c: Coincident(g59,g62)
    c: Coincident(g61,g62)
    c: Coincident(g68,g71)
    c: Coincident(g70,g71)
    c: Coincident(g29,g30)
    c: Coincident(g28,g29)
    c: Coincident(g27,g28)
    c: Coincident(g26,g27)
    c: Coincident(g2,g48)
    c: Coincident(g0,g2)
    c: Coincident(g22,g23)
    c: Coincident(g23,g24)
    c: Coincident(g0,g1)
    c: Coincident(g21,g22)
    c: Coincident(g24,g25)
    c: Coincident(g25,g26)
    c: Coincident(g53,g54)
    c: Coincident(g52,g53)
    c: Coincident(g68,g69)
    c: Coincident(g69,g70)
    c: Coincident(g55,g56)
    c: Coincident(g54,g55)
    c: Coincident(g50,g51)
    c: Coincident(g51,g52)
    c: Coincident(g1,g3)
    c: Coincident(g50,g58)
    c: Coincident(g4,g5)
    c: Coincident(g3,g4)
    c: Coincident(g59,g60)
    c: Coincident(g60,g61)
    c: Coincident(g56,g57)
    c: Coincident(g57,g58)
    c: Coincident(g17,g18)
    c: Coincident(g16,g17)
    c: Coincident(g20,g21)
    c: Coincident(g19,g20)
    c: Coincident(g18,g19)
    c: Coincident(g5,g6)
    c: Coincident(g14,g15)
    c: Coincident(g15,g16)
    c: Coincident(g7,g8)
    c: Coincident(g6,g7)
    c: Coincident(g13,g14)
    c: Coincident(g12,g13)
    c: Coincident(g8,g9)
    c: Coincident(g11,g12)
    c: Coincident(g10,g11)
    c: Coincident(g9,g10)
    c: Block(g0)
    c: Block(g1)
    c: Block(g2)
    c: Block(g3)
    c: Block(g4)
    c: Block(g5)
    c: Block(g6)
    c: Block(g7)
    c: Block(g8)
    c: Block(g9)
    c: Block(g10)
    c: Block(g11)
    c: Block(g12)
    c: Block(g13)
    c: Block(g14)
    c: Block(g15)
    c: Block(g16)
    c: Block(g17)
    c: Block(g18)
    c: Block(g19)
    c: Block(g20)
    c: Block(g21)
    c: Block(g22)
    c: Block(g23)
    c: Block(g24)
    c: Block(g25)
    c: Block(g26)
    c: Block(g27)
    c: Block(g28)
    c: Block(g29)
    c: Block(g30)
    c: Block(g31)
    c: Block(g32)
    c: Block(g33)
    c: Block(g34)
    c: Block(g35)
    c: Block(g36)
    c: Block(g37)
    c: Block(g38)
    c: Block(g39)
    c: Block(g40)
    c: Block(g41)
    c: Block(g42)
    c: Block(g43)
    c: Block(g44)
    c: Block(g45)
    c: Block(g46)
    c: Block(g47)
    c: Block(g48)
    c: Block(g49)
    c: Block(g50)
    c: Block(g51)
    c: Block(g52)
    c: Block(g53)
    c: Block(g54)
    c: Block(g55)
    c: Block(g56)
    c: Block(g57)
    c: Block(g58)
    c: Block(g59)
    c: Block(g60)
    c: Block(g61)
    c: Block(g62)
    c: Block(g63)
    c: Block(g64)
    c: Block(g65)
    c: Block(g66)
    c: Block(g67)
    c: Block(g68)
    c: Block(g69)
    c: Block(g70)
    c: Block(g71)
    c: Block(g72)
    c: Block(g73)
FEATURE [Sketcher::SketchObject] Sketch031
  ArcFitTolerance = 1e-06
  AttachmentOffset = pos=(0,0,-5.1) rot=(0,0,1;0rad)
  AttachmentSupport = -> [XY_Plane005]
  ExternalTypes = [0]
  FullyConstrained = false
  MakeInternals = false
  MapMode = 5
  Placement = pos=(0,0,-5.1) rot=(0,0,1;0rad)
  _ExternalGeoVersion = 0
  sketch-geometry (100):
    g0: ArcOfCircle [constr] CenterX=45.3 CenterY=2.4 CenterZ=0 NormalX=-1e-16 NormalY=0 NormalZ=1 AngleXU=1.5708 Radius=1.5 StartAngle=0 EndAngle=1.22777
    g1: LineSegment [constr] StartX=59.4 StartY=3.9 StartZ=0 EndX=45.3 EndY=3.9 EndZ=0
    g2: LineSegment [constr] StartX=43.8874 StartY=2.9045 StartZ=0 EndX=43.8874 EndY=2.8 EndZ=0
    g3: ArcOfCircle [constr] CenterX=59.4 CenterY=2.4 CenterZ=0 NormalX=-1e-16 NormalY=0 NormalZ=1 AngleXU=3.90995e-07 Radius=1.5 StartAngle=0 EndAngle=1.5708
    g4: LineSegment [constr] StartX=60.9 StartY=-0.4 StartZ=0 EndX=60.9 EndY=2.4 EndZ=0
    g5: LineSegment [constr] StartX=76.4 StartY=-0.4 StartZ=0 EndX=60.9 EndY=-0.4 EndZ=0
    g6: ArcOfCircle [constr] CenterX=76.4 CenterY=-1.9 CenterZ=0 NormalX=-1e-16 NormalY=0 NormalZ=1 AngleXU=3.90995e-07 Radius=1.5 StartAngle=0 EndAngle=1.5708
    g7: LineSegment [constr] StartX=77.9 StartY=-6.3 StartZ=0 EndX=77.9 EndY=-1.9 EndZ=0
    g8: LineSegment [constr] StartX=96.4 StartY=-6.3 StartZ=0 EndX=77.9 EndY=-6.3 EndZ=0
    g9: ArcOfCircle [constr] CenterX=96.4 CenterY=-7.8 CenterZ=0 NormalX=-1e-16 NormalY=0 NormalZ=1 AngleXU=3.90995e-07 Radius=1.5 StartAngle=0 EndAngle=1.5708
    g10: LineSegment [constr] StartX=97.9 StartY=-59.8 StartZ=0 EndX=97.9 EndY=-7.8 EndZ=0
    g11: LineSegment [constr] StartX=97.9 StartY=-72.8 StartZ=0 EndX=97.9 EndY=-59.8 EndZ=0
    g12: ArcOfCircle [constr] CenterX=96.4 CenterY=-72.8 CenterZ=0 NormalX=-1e-16 NormalY=0 NormalZ=1 AngleXU=-1.5708 Radius=1.5 StartAngle=0 EndAngle=1.5708
    g13: LineSegment [constr] StartX=78 StartY=-74.3 StartZ=0 EndX=96.4 EndY=-74.3 EndZ=0
    g14: ArcOfCircle [constr] CenterX=78 CenterY=-72.8 CenterZ=0 NormalX=-1e-16 NormalY=0 NormalZ=1 AngleXU=-3.14159 Radius=1.5 StartAngle=0 EndAngle=1.5708
    g15: LineSegment [constr] StartX=76.5 StartY=-68.4 StartZ=0 EndX=76.5 EndY=-72.8 EndZ=0
    g16: LineSegment [constr] StartX=68.6 StartY=-68.4 StartZ=0 EndX=76.5 EndY=-68.4 EndZ=0
    g17: LineSegment [constr] StartX=43.1 StartY=-66.1 StartZ=0 EndX=49.65 EndY=-66.1 EndZ=0
    g18: LineSegment [constr] StartX=43.1 StartY=-71.2 StartZ=0 EndX=43.1 EndY=-66.1 EndZ=0
    g19: ArcOfCircle [constr] CenterX=41.6 CenterY=-71.2 CenterZ=0 NormalX=-1e-16 NormalY=0 NormalZ=1 AngleXU=-1.5708 Radius=1.5 StartAngle=0 EndAngle=1.5708
    g20: LineSegment [constr] StartX=41.4 StartY=-72.7 StartZ=0 EndX=41.6 EndY=-72.7 EndZ=0
    g21: LineSegment [constr] StartX=24.227 StartY=-72.7043 StartZ=0 EndX=41.4 EndY=-72.7 EndZ=0
    g22: LineSegment [constr] StartX=6.18739 StartY=-75.9853 StartZ=0 EndX=24.227 EndY=-72.7043 EndZ=0
    g23: LineSegment [constr] StartX=-12.4977 StartY=-82.7894 StartZ=0 EndX=6.18739 EndY=-75.9853 EndZ=0
    g24: ArcOfCircle [constr] CenterX=-13.011 CenterY=-81.3799 CenterZ=0 NormalX=-1e-16 NormalY=0 NormalZ=1 AngleXU=-2.78726 Radius=1.5 StartAngle=0 EndAngle=1.56568
    g25: LineSegment [constr] StartX=-22.1 StartY=-61.1344 StartZ=0 EndX=-14.4178 EndY=-81.9004 EndZ=0
    g26: LineSegment [constr] StartX=-22.1 StartY=0 StartZ=0 EndX=-22.1 EndY=-61.1344 EndZ=0
    g27: LineSegment [constr] StartX=9.9 StartY=0 StartZ=0 EndX=5 EndY=0 EndZ=0
    g28: LineSegment [constr] StartX=9.9 StartY=1.3 StartZ=0 EndX=9.9 EndY=0 EndZ=0
    g29: LineSegment [constr] StartX=23.7 StartY=1.3 StartZ=0 EndX=9.9 EndY=1.3 EndZ=0
    g30: ArcOfCircle [constr] CenterX=25.2 CenterY=1.3 CenterZ=0 NormalX=-1e-16 NormalY=0 NormalZ=1 AngleXU=1.5708 Radius=1.5 StartAngle=0 EndAngle=1.5708
    g31: LineSegment [constr] StartX=43.8874 StartY=2.8 StartZ=0 EndX=25.2 EndY=2.8 EndZ=0
    g32: Circle [constr] CenterX=95.6 CenterY=-57.3 CenterZ=0 NormalX=-1e-16 NormalY=0 NormalZ=1 AngleXU=-1.5708 Radius=1.1
    g33: ArcOfCircle [constr] CenterX=60.7 CenterY=-66.9 CenterZ=0 NormalX=-1e-16 NormalY=0 NormalZ=1 AngleXU=-3.14159 Radius=1.5 StartAngle=0 EndAngle=1.5708
    g34: LineSegment [constr] StartX=59.2 StartY=-66.1 StartZ=0 EndX=59.2 EndY=-66.9 EndZ=0
    g35: LineSegment [constr] StartX=51.15 StartY=-66.1 StartZ=0 EndX=59.2 EndY=-66.1 EndZ=0
    g36: LineSegment [constr] StartX=60.7 StartY=-68.4 StartZ=0 EndX=67.1 EndY=-68.4 EndZ=0
    g37: LineSegment [constr] StartX=62.7 StartY=-60 StartZ=0 EndX=27.8 EndY=-60 EndZ=0
    g38: LineSegment [constr] StartX=62.7 StartY=-57.6 StartZ=0 EndX=62.7 EndY=-60 EndZ=0
    g39: LineSegment [constr] StartX=27.8 StartY=-57.6 StartZ=0 EndX=62.7 EndY=-57.6 EndZ=0
    g40: LineSegment [constr] StartX=27.8 StartY=-60 StartZ=0 EndX=27.8 EndY=-57.6 EndZ=0
    g41: Circle [constr] CenterX=-14 CenterY=-73.8 CenterZ=0 NormalX=-1e-16 NormalY=0 NormalZ=1 AngleXU=-1.5708 Radius=1.1
    g42: LineSegment [constr] StartX=-14.8 StartY=-64.1 StartZ=0 EndX=-16.4 EndY=-64.1 EndZ=0
    g43: LineSegment [constr] StartX=-14.8 StartY=-54 StartZ=0 EndX=-14.8 EndY=-64.1 EndZ=0
    g44: LineSegment [constr] StartX=-16.4 StartY=-54 StartZ=0 EndX=-14.8 EndY=-54 EndZ=0
    g45: LineSegment [constr] StartX=-16.4 StartY=-64.1 StartZ=0 EndX=-16.4 EndY=-54 EndZ=0
    g46: LineSegment [constr] StartX=52 StartY=-56.2 StartZ=0 EndX=27.8 EndY=-56.2 EndZ=0
    g47: LineSegment [constr] StartX=52 StartY=-53.8 StartZ=0 EndX=52 EndY=-56.2 EndZ=0
    g48: LineSegment [constr] StartX=27.8 StartY=-53.8 StartZ=0 EndX=52 EndY=-53.8 EndZ=0
    g49: LineSegment [constr] StartX=27.8 StartY=-56.2 StartZ=0 EndX=27.8 EndY=-53.8 EndZ=0
    g50: Circle [constr] CenterX=95.6 CenterY=-23.3 CenterZ=0 NormalX=-1e-16 NormalY=0 NormalZ=1 AngleXU=-1.5708 Radius=1.1
    g51: Circle [constr] CenterX=25.9 CenterY=0.6 CenterZ=0 NormalX=-1e-16 NormalY=0 NormalZ=1 AngleXU=-1.5708 Radius=1.1
    g52: LineSegment [constr] StartX=49.65 StartY=-66.1 StartZ=0 EndX=51.15 EndY=-66.1 EndZ=0
    g53: LineSegment [constr] StartX=67.1 StartY=-68.4 StartZ=0 EndX=68.6 EndY=-68.4 EndZ=0
    g54: LineSegment [constr] StartX=-22.1 StartY=0 StartZ=0 EndX=5 EndY=0 EndZ=0
    g55: LineSegment StartX=-22.1 StartY=0.3 StartZ=0 EndX=5 EndY=0.3 EndZ=0
    g56: LineSegment StartX=9.6 StartY=0.3 StartZ=0 EndX=5 EndY=0.3 EndZ=0
    g57: LineSegment StartX=9.6 StartY=1.3 StartZ=0 EndX=9.6 EndY=0.3 EndZ=0
    g58: ArcOfCircle CenterX=9.9 CenterY=1.3 CenterZ=0 NormalX=0 NormalY=0 NormalZ=1 AngleXU=0 Radius=0.3 StartAngle=1.5708 EndAngle=3.14159
    g59: LineSegment StartX=23.4252 StartY=1.6 StartZ=0 EndX=9.9 EndY=1.6 EndZ=0
    g60: ArcOfCircle CenterX=25.2 CenterY=1.3 CenterZ=0 NormalX=0 NormalY=0 NormalZ=1 AngleXU=1.5708 Radius=1.8 StartAngle=0 EndAngle=1.40335
    g61: LineSegment StartX=43.6417 StartY=3.1 StartZ=0 EndX=25.2 EndY=3.1 EndZ=0
    g62: ArcOfCircle CenterX=45.3 CenterY=2.4 CenterZ=0 NormalX=0 NormalY=0 NormalZ=1 AngleXU=1.5708 Radius=1.8 StartAngle=0 EndAngle=1.17137
    g63: LineSegment StartX=59.4 StartY=4.2 StartZ=0 EndX=45.3 EndY=4.2 EndZ=0
    g64: ArcOfCircle CenterX=59.4 CenterY=2.4 CenterZ=0 NormalX=0 NormalY=0 NormalZ=1 AngleXU=3.90995e-07 Radius=1.8 StartAngle=-1.8e-15 EndAngle=1.5708
    g65: LineSegment StartX=61.2 StartY=-0.1 StartZ=0 EndX=61.2 EndY=2.4 EndZ=0
    g66: LineSegment StartX=76.4 StartY=-0.1 StartZ=0 EndX=61.2 EndY=-0.1 EndZ=0
    g67: ArcOfCircle CenterX=76.4 CenterY=-1.9 CenterZ=0 NormalX=0 NormalY=0 NormalZ=1 AngleXU=3.90995e-07 Radius=1.8 StartAngle=-1.8e-15 EndAngle=1.5708
    g68: LineSegment StartX=78.2 StartY=-6 StartZ=0 EndX=78.2 EndY=-1.9 EndZ=0
    g69: LineSegment StartX=113.4 StartY=-6 StartZ=0 EndX=78.2 EndY=-6 EndZ=0
    g70: ArcOfCircle CenterX=113.4 CenterY=-7.8 CenterZ=0 NormalX=0 NormalY=0 NormalZ=1 AngleXU=3.90995e-07 Radius=1.8 StartAngle=6.28318 EndAngle=7.85398
    g71: LineSegment StartX=115.2 StartY=-56.6961 StartZ=0 EndX=115.2 EndY=-7.8 EndZ=0
    g72: LineSegment StartX=115.2 StartY=-72.8 StartZ=0 EndX=115.2 EndY=-56.6961 EndZ=0
    g73: ArcOfCircle CenterX=113.4 CenterY=-72.8 CenterZ=0 NormalX=0 NormalY=0 NormalZ=1 AngleXU=-1.5708 Radius=1.8 StartAngle=6.28318 EndAngle=7.85398
    g74: LineSegment StartX=78 StartY=-74.6 StartZ=0 EndX=113.4 EndY=-74.6 EndZ=0
    g75: ArcOfCircle CenterX=78 CenterY=-72.8 CenterZ=0 NormalX=0 NormalY=0 NormalZ=1 AngleXU=-3.14159 Radius=1.8 StartAngle=-1.8e-15 EndAngle=1.5708
    g76: LineSegment StartX=76.2 StartY=-68.7 StartZ=0 EndX=76.2 EndY=-72.8 EndZ=0
    g77: LineSegment StartX=68.6 StartY=-68.7 StartZ=0 EndX=76.2 EndY=-68.7 EndZ=0
    g78: LineSegment StartX=67.1 StartY=-68.7 StartZ=0 EndX=68.6 EndY=-68.7 EndZ=0
    g79: LineSegment StartX=60.7 StartY=-68.7 StartZ=0 EndX=67.1 EndY=-68.7 EndZ=0
    g80: ArcOfCircle CenterX=60.7 CenterY=-66.9 CenterZ=0 NormalX=0 NormalY=0 NormalZ=1 AngleXU=-3.14159 Radius=1.8 StartAngle=0 EndAngle=1.5708
    g81: LineSegment StartX=58.9 StartY=-66.4 StartZ=0 EndX=58.9 EndY=-66.9 EndZ=0
    g82: LineSegment StartX=51.15 StartY=-66.4 StartZ=0 EndX=58.9 EndY=-66.4 EndZ=0
    g83: LineSegment StartX=49.65 StartY=-66.4 StartZ=0 EndX=51.15 EndY=-66.4 EndZ=0
    g84: LineSegment StartX=43.4 StartY=-66.4 StartZ=0 EndX=49.65 EndY=-66.4 EndZ=0
    g85: LineSegment StartX=43.4 StartY=-71.2 StartZ=0 EndX=43.4 EndY=-66.4 EndZ=0
    g86: ArcOfCircle CenterX=41.6 CenterY=-71.2 CenterZ=0 NormalX=0 NormalY=0 NormalZ=1 AngleXU=-1.5708 Radius=1.8 StartAngle=0 EndAngle=1.5708
    g87: LineSegment StartX=41.4 StartY=-73 StartZ=0 EndX=41.6 EndY=-73 EndZ=0
    g88: LineSegment StartX=24.2541 StartY=-73.0043 StartZ=0 EndX=41.4 EndY=-73 EndZ=0
    g89: LineSegment StartX=6.26611 StartY=-76.2759 StartZ=0 EndX=24.2541 EndY=-73.0043 EndZ=0
    g90: LineSegment StartX=-12.3951 StartY=-83.0713 StartZ=0 EndX=6.26611 EndY=-76.2759 EndZ=0
    g91: ArcOfCircle CenterX=-13.011 CenterY=-81.3799 CenterZ=0 NormalX=0 NormalY=0 NormalZ=1 AngleXU=-2.78726 Radius=1.8 StartAngle=6.28319 EndAngle=7.84887
    g92: LineSegment StartX=-22.3814 StartY=-61.2385 StartZ=0 EndX=-14.6992 EndY=-82.0044 EndZ=0
    g93: ArcOfCircle CenterX=-22.1 CenterY=-61.1344 CenterZ=0 NormalX=0 NormalY=0 NormalZ=1 AngleXU=1.5708 Radius=0.3 StartAngle=1.5708 EndAngle=1.92513
    g94: LineSegment StartX=-22.4 StartY=0 StartZ=0 EndX=-22.4 EndY=-61.1344 EndZ=0
    g95: ArcOfCircle CenterX=-22.1 CenterY=0 CenterZ=0 NormalX=0 NormalY=0 NormalZ=1 AngleXU=0 Radius=0.3 StartAngle=1.5708 EndAngle=3.14159
    g96: LineSegment [constr] StartX=113.4 StartY=-72.8 StartZ=0 EndX=115.2 EndY=-72.8 EndZ=0
    g97: LineSegment [constr] StartX=113.4 StartY=-7.8 StartZ=0 EndX=113.4 EndY=-6 EndZ=0
    g98: LineSegment [constr] StartX=113.4 StartY=-7.8 StartZ=0 EndX=115.2 EndY=-7.8 EndZ=0
    g99: LineSegment [constr] StartX=113.4 StartY=-72.8 StartZ=0 EndX=113.4 EndY=-74.6 EndZ=0
  constraints (169):
    c: Coincident(g25,g26)
    c: Coincident(g42,g45)
    c: Coincident(g44,g45)
    c: Coincident(g42,g43)
    c: Coincident(g43,g44)
    c: Coincident(g24,g25)
    c: Coincident(g23,g24)
    c: Coincident(g22,g23)
    c: Coincident(g27,g28)
    c: Coincident(g28,g29)
    c: Coincident(g29,g30)
    c: Coincident(g21,g22)
    c: Coincident(g30,g31)
    c: Coincident(g37,g40)
    c: Coincident(g39,g40)
    c: Coincident(g46,g49)
    c: Coincident(g48,g49)
    c: Coincident(g20,g21)
    c: Coincident(g19,g20)
    c: Coincident(g18,g19)
    c: Coincident(g17,g18)
    c: Coincident(g2,g31)
    c: Coincident(g0,g2)
    c: Coincident(g0,g1)
    c: Coincident(g46,g47)
    c: Coincident(g47,g48)
    c: Coincident(g33,g34)
    c: Coincident(g34,g35)
    c: Coincident(g1,g3)
    c: Coincident(g33,g36)
    c: Coincident(g4,g5)
    c: Coincident(g3,g4)
    c: Coincident(g37,g38)
    c: Coincident(g38,g39)
    c: Coincident(g5,g6)
    c: Coincident(g14,g15)
    c: Coincident(g15,g16)
    c: Coincident(g7,g8)
    c: Coincident(g6,g7)
    c: Coincident(g13,g14)
    c: Coincident(g12,g13)
    c: Coincident(g8,g9)
    c: Coincident(g11,g12)
    c: Coincident(g10,g11)
    c: Coincident(g9,g10)
    c: Block(g0)
    c: Block(g1)
    c: Block(g2)
    c: Block(g3)
    c: Block(g4)
    c: Block(g5)
    c: Block(g6)
    c: Block(g7)
    c: Block(g8)
    c: Block(g9)
    c: Block(g10)
    c: Block(g11)
    c: Block(g12)
    c: Block(g13)
    c: Block(g14)
    c: Block(g15)
    c: Block(g16)
    c: Block(g17)
    c: Block(g18)
    c: Block(g19)
    c: Block(g20)
    c: Block(g21)
    c: Block(g22)
    c: Block(g23)
    c: Block(g24)
    c: Block(g25)
    c: Block(g26)
    c: Block(g27)
    c: Block(g28)
    c: Block(g29)
    c: Block(g30)
    c: Block(g31)
    c: Block(g32)
    c: Block(g33)
    c: Block(g34)
    c: Block(g35)
    c: Block(g36)
    c: Block(g37)
    c: Block(g38)
    c: Block(g39)
    c: Block(g40)
    c: Block(g41)
    c: Block(g42)
    c: Block(g43)
    c: Block(g44)
    c: Block(g45)
    c: Block(g46)
    c: Block(g47)
    c: Block(g48)
    c: Block(g49)
    c: Block(g50)
    c: Block(g51)
    c: Coincident(g52,g17)
    c: Coincident(g52,g35)
    c: Horizontal(g52)
    c: Coincident(g53,g36)
    c: Coincident(g53,g16)
    c: Horizontal(g53)
    c: Coincident(g54,g26)
    c: Coincident(g54,g27)
    c: Horizontal(g54)
    c: Coincident(g55,g56)
    c: Tangent(g55,g95) = 1.5708
    c: Coincident(g56,g57)
    c: Tangent(g57,g58) = -1.5708
    c: Tangent(g58,g59) = -1.5708
    c: Coincident(g59,g60)
    c: Coincident(g61,g62)
    c: Coincident(g62,g63)
    c: Coincident(g65,g66)
    c: Coincident(g68,g69)
    c: Coincident(g71,g72)
    c: Coincident(g76,g77)
    c: Coincident(g77,g78)
    c: Coincident(g78,g79)
    c: Coincident(g81,g82)
    c: Coincident(g82,g83)
    c: Coincident(g83,g84)
    c: Coincident(g84,g85)
    c: Coincident(g87,g88)
    c: Coincident(g88,g89)
    c: Coincident(g89,g90)
    c: Tangent(g92,g93) = -1.5708
    c: Tangent(g93,g94) = -1.5708
    c: Tangent(g94,g95) = -1.5708
    c: Coincident(g91,g92)
    c: Coincident(g90,g91)
    c: Coincident(g60,g61)
    c: Coincident(g86,g87)
    c: Coincident(g85,g86)
    c: Coincident(g80,g81)
    c: Coincident(g63,g64)
    c: Coincident(g79,g80)
    c: Coincident(g64,g65)
    c: Coincident(g66,g67)
    c: Coincident(g74,g75)
    c: Coincident(g67,g68)
    c: Coincident(g73,g74)
    c: Coincident(g69,g70)
    c: Coincident(g72,g73)
    c: Coincident(g70,g71)
    c: Block(g75)
    c: Block(g68)
    c: Block(g76)
    c: Vertical(g72)
    c: Vertical(g71)
    c: Horizontal(g69)
    c: Horizontal(g74)
    c: DistanceX(g74,g74) = 35.4
    c: DistanceX(g69,g69) = 35.2
    c: Radius(g73) = 1.8
    c: Radius(g70) = 1.8
    c: Coincident(g96,g73)
    c: Coincident(g96,g72)
    c: Coincident(g97,g70)
    c: Coincident(g97,g69)
    c: Coincident(g98,g70)
    c: Coincident(g98,g70)
    c: Coincident(g99,g73)
    c: Coincident(g99,g73)
    c: Vertical(g99)
    c: Horizontal(g96)
    c: Vertical(g97)
    c: Horizontal(g98)
FEATURE [PartDesign::Pocket] Pocket013
  BaseFeature = -> Pad011
  Direction = (0,0,-1)
  Length = 10
  Length2 = 5
  Profile = -> Sketch031
  ReferenceAxis = -> Sketch031 [N_Axis]
  Refine = true
  Reversed = true
  SideType = 0
  Suppressed = false
  Type = 0
  Type2 = 0
FEATURE [Sketcher::SketchObject] Sketch032
  ArcFitTolerance = 1e-06
  AttachmentOffset = pos=(0,0,-5.1) rot=(0,0,1;0rad)
  AttachmentSupport = -> [XY_Plane005]
  ExternalTypes = [0]
  FullyConstrained = false
  MakeInternals = false
  MapMode = 5
  Placement = pos=(0,0,-5.1) rot=(0,0,1;0rad)
  _ExternalGeoVersion = 0
  sketch-geometry (4):
    g0: LineSegment StartX=9.9 StartY=0 StartZ=0 EndX=9.9 EndY=7.12941 EndZ=0
    g1: LineSegment StartX=9.9 StartY=7.12941 StartZ=0 EndX=2.38364 EndY=7.12941 EndZ=0
    g2: LineSegment StartX=2.38364 StartY=7.12941 StartZ=0 EndX=2.38364 EndY=0 EndZ=0
    g3: LineSegment StartX=2.38364 StartY=0 StartZ=0 EndX=9.9 EndY=0 EndZ=0
  constraints (10):
    c: Coincident(g0,g1)
    c: Coincident(g1,g2)
    c: Coincident(g2,g3)
    c: Coincident(g3,g0)
    c: Vertical(g0)
    c: Vertical(g2)
    c: Horizontal(g1)
    c: Horizontal(g3)
    c: DistanceX(g-1,g0) = 9.9
    c: PointOnObject(g2,g-1)
FEATURE [PartDesign::Pocket] Pocket014
  BaseFeature = -> Pocket013
  Direction = (0,0,-1)
  Length = 10
  Length2 = 10
  Profile = -> Sketch032
  ReferenceAxis = -> Sketch032 [N_Axis]
  Refine = true
  SideType = 1
  Suppressed = false
  Type = 0
  Type2 = 0
FEATURE [Sketcher::SketchObject] Sketch033
  ArcFitTolerance = 1e-06
  AttachmentSupport = -> [XY_Plane005]
  ExternalTypes = [0]
  FullyConstrained = false
  MakeInternals = false
  MapMode = 5
  _ExternalGeoVersion = 0
  sketch-geometry (79):
    g0: ArcOfCircle [constr] CenterX=45.3 CenterY=2.4 CenterZ=0 NormalX=-1e-16 NormalY=0 NormalZ=1 AngleXU=1.5708 Radius=1.5 StartAngle=0 EndAngle=1.22777
    g1: LineSegment [constr] StartX=59.4 StartY=3.9 StartZ=0 EndX=45.3 EndY=3.9 EndZ=0
    g2: LineSegment [constr] StartX=43.8874 StartY=2.9045 StartZ=0 EndX=43.8874 EndY=2.8 EndZ=0
    g3: ArcOfCircle [constr] CenterX=59.4 CenterY=2.4 CenterZ=0 NormalX=-1e-16 NormalY=0 NormalZ=1 AngleXU=3.90995e-07 Radius=1.5 StartAngle=0 EndAngle=1.5708
    g4: LineSegment [constr] StartX=60.9 StartY=-0.4 StartZ=0 EndX=60.9 EndY=2.4 EndZ=0
    g5: LineSegment [constr] StartX=76.4 StartY=-0.4 StartZ=0 EndX=60.9 EndY=-0.4 EndZ=0
    g6: ArcOfCircle [constr] CenterX=76.4 CenterY=-1.9 CenterZ=0 NormalX=-1e-16 NormalY=0 NormalZ=1 AngleXU=3.90995e-07 Radius=1.5 StartAngle=0 EndAngle=1.5708
    g7: LineSegment [constr] StartX=77.9 StartY=-6.3 StartZ=0 EndX=77.9 EndY=-1.9 EndZ=0
    g8: LineSegment [constr] StartX=96.4 StartY=-6.3 StartZ=0 EndX=77.9 EndY=-6.3 EndZ=0
    g9: ArcOfCircle [constr] CenterX=96.4 CenterY=-7.8 CenterZ=0 NormalX=-1e-16 NormalY=0 NormalZ=1 AngleXU=3.90995e-07 Radius=1.5 StartAngle=0 EndAngle=1.5708
    g10: LineSegment [constr] StartX=97.9 StartY=-59.8 StartZ=0 EndX=97.9 EndY=-7.8 EndZ=0
    g11: LineSegment [constr] StartX=97.9 StartY=-72.8 StartZ=0 EndX=97.9 EndY=-59.8 EndZ=0
    g12: ArcOfCircle [constr] CenterX=96.4 CenterY=-72.8 CenterZ=0 NormalX=-1e-16 NormalY=0 NormalZ=1 AngleXU=-1.5708 Radius=1.5 StartAngle=0 EndAngle=1.5708
    g13: LineSegment [constr] StartX=78 StartY=-74.3 StartZ=0 EndX=96.4 EndY=-74.3 EndZ=0
    g14: ArcOfCircle [constr] CenterX=78 CenterY=-72.8 CenterZ=0 NormalX=-1e-16 NormalY=0 NormalZ=1 AngleXU=-3.14159 Radius=1.5 StartAngle=0 EndAngle=1.5708
    g15: LineSegment [constr] StartX=76.5 StartY=-68.4 StartZ=0 EndX=76.5 EndY=-72.8 EndZ=0
    g16: LineSegment [constr] StartX=68.6 StartY=-68.4 StartZ=0 EndX=76.5 EndY=-68.4 EndZ=0
    g17: LineSegment [constr] StartX=68.6 StartY=-69.9 StartZ=0 EndX=68.6 EndY=-68.4 EndZ=0
    g18: LineSegment [constr] StartX=75 StartY=-69.9 StartZ=0 EndX=68.6 EndY=-69.9 EndZ=0
    g19: LineSegment [constr] StartX=75 StartY=-72.8 StartZ=0 EndX=75 EndY=-69.9 EndZ=0
    g20: ArcOfCircle [constr] CenterX=73.5 CenterY=-72.8 CenterZ=0 NormalX=-1e-16 NormalY=0 NormalZ=1 AngleXU=-1.5708 Radius=1.5 StartAngle=0 EndAngle=1.5708
    g21: LineSegment [constr] StartX=46.1 StartY=-74.3 StartZ=0 EndX=73.5 EndY=-74.3 EndZ=0
    g22: ArcOfCircle [constr] CenterX=46.1 CenterY=-72.8 CenterZ=0 NormalX=-1e-16 NormalY=0 NormalZ=1 AngleXU=-3.14159 Radius=1.5 StartAngle=0 EndAngle=1.5708
    g23: LineSegment [constr] StartX=44.6 StartY=-67.6 StartZ=0 EndX=44.6 EndY=-72.8 EndZ=0
    g24: LineSegment [constr] StartX=49.65 StartY=-67.6 StartZ=0 EndX=44.6 EndY=-67.6 EndZ=0
    g25: LineSegment [constr] StartX=49.65 StartY=-66.1 StartZ=0 EndX=49.65 EndY=-67.6 EndZ=0
    g26: LineSegment [constr] StartX=43.1 StartY=-66.1 StartZ=0 EndX=49.65 EndY=-66.1 EndZ=0
    g27: LineSegment [constr] StartX=43.1 StartY=-71.2 StartZ=0 EndX=43.1 EndY=-66.1 EndZ=0
    g28: ArcOfCircle [constr] CenterX=41.6 CenterY=-71.2 CenterZ=0 NormalX=-1e-16 NormalY=0 NormalZ=1 AngleXU=-1.5708 Radius=1.5 StartAngle=0 EndAngle=1.5708
    g29: LineSegment [constr] StartX=41.4 StartY=-72.7 StartZ=0 EndX=41.6 EndY=-72.7 EndZ=0
    g30: LineSegment [constr] StartX=24.227 StartY=-72.7043 StartZ=0 EndX=41.4 EndY=-72.7 EndZ=0
    g31: LineSegment [constr] StartX=6.18739 StartY=-75.9853 StartZ=0 EndX=24.227 EndY=-72.7043 EndZ=0
    g32: LineSegment [constr] StartX=-12.4977 StartY=-82.7894 StartZ=0 EndX=6.18739 EndY=-75.9853 EndZ=0
    g33: ArcOfCircle [constr] CenterX=-13.011 CenterY=-81.3799 CenterZ=0 NormalX=-1e-16 NormalY=0 NormalZ=1 AngleXU=-2.78726 Radius=1.5 StartAngle=0 EndAngle=1.56568
    g34: LineSegment [constr] StartX=-22.1 StartY=-61.1344 StartZ=0 EndX=-14.4178 EndY=-81.9004 EndZ=0
    g35: LineSegment [constr] StartX=-22.1 StartY=0 StartZ=0 EndX=-22.1 EndY=-61.1344 EndZ=0
    g36: LineSegment [constr] StartX=-16.4 StartY=0 StartZ=0 EndX=-22.1 EndY=0 EndZ=0
    g37: LineSegment [constr] StartX=-16.4 StartY=-10.5 StartZ=0 EndX=-16.4 EndY=0 EndZ=0
    g38: LineSegment [constr] StartX=-14.8 StartY=-10.5 StartZ=0 EndX=-16.4 EndY=-10.5 EndZ=0
    g39: LineSegment [constr] StartX=-14.8 StartY=0 StartZ=0 EndX=-14.8 EndY=-10.5 EndZ=0
    g40: LineSegment [constr] StartX=-5 StartY=0 StartZ=0 EndX=-14.8 EndY=0 EndZ=0
    g41: LineSegment [constr] StartX=-5 StartY=-4 StartZ=0 EndX=-5 EndY=0 EndZ=0
    g42: LineSegment [constr] StartX=5 StartY=-4 StartZ=0 EndX=-5 EndY=-4 EndZ=0
    g43: LineSegment [constr] StartX=5 StartY=0 StartZ=0 EndX=5 EndY=-4 EndZ=0
    g44: LineSegment [constr] StartX=9.9 StartY=0 StartZ=0 EndX=5 EndY=0 EndZ=0
    g45: LineSegment [constr] StartX=9.9 StartY=1.3 StartZ=0 EndX=9.9 EndY=0 EndZ=0
    g46: LineSegment [constr] StartX=23.7 StartY=1.3 StartZ=0 EndX=9.9 EndY=1.3 EndZ=0
    g47: ArcOfCircle [constr] CenterX=25.2 CenterY=1.3 CenterZ=0 NormalX=-1e-16 NormalY=0 NormalZ=1 AngleXU=1.5708 Radius=1.5 StartAngle=0 EndAngle=1.5708
    g48: LineSegment [constr] StartX=43.8874 StartY=2.8 StartZ=0 EndX=25.2 EndY=2.8 EndZ=0
    g49: Circle [constr] CenterX=112.6 CenterY=-57.3 CenterZ=0 NormalX=-1e-16 NormalY=0 NormalZ=1 AngleXU=-1.5708 Radius=1.1
    g50: ArcOfCircle [constr] CenterX=60.7 CenterY=-66.9 CenterZ=0 NormalX=-1e-16 NormalY=0 NormalZ=1 AngleXU=-3.14159 Radius=1.5 StartAngle=0 EndAngle=1.5708
    g51: LineSegment [constr] StartX=59.2 StartY=-66.1 StartZ=0 EndX=59.2 EndY=-66.9 EndZ=0
    g52: LineSegment [constr] StartX=51.15 StartY=-66.1 StartZ=0 EndX=59.2 EndY=-66.1 EndZ=0
    g53: LineSegment [constr] StartX=51.15 StartY=-67.6 StartZ=0 EndX=51.15 EndY=-66.1 EndZ=0
    g54: LineSegment [constr] StartX=56.7 StartY=-67.6 StartZ=0 EndX=51.15 EndY=-67.6 EndZ=0
    g55: LineSegment [constr] StartX=56.7 StartY=-69.9 StartZ=0 EndX=56.7 EndY=-67.6 EndZ=0
    g56: LineSegment [constr] StartX=67.1 StartY=-69.9 StartZ=0 EndX=56.7 EndY=-69.9 EndZ=0
    g57: LineSegment [constr] StartX=67.1 StartY=-68.4 StartZ=0 EndX=67.1 EndY=-69.9 EndZ=0
    g58: LineSegment [constr] StartX=60.7 StartY=-68.4 StartZ=0 EndX=67.1 EndY=-68.4 EndZ=0
    g59: LineSegment [constr] StartX=62.7 StartY=-60 StartZ=0 EndX=27.8 EndY=-60 EndZ=0
    g60: LineSegment [constr] StartX=62.7 StartY=-57.6 StartZ=0 EndX=62.7 EndY=-60 EndZ=0
    g61: LineSegment [constr] StartX=27.8 StartY=-57.6 StartZ=0 EndX=62.7 EndY=-57.6 EndZ=0
    g62: LineSegment [constr] StartX=27.8 StartY=-60 StartZ=0 EndX=27.8 EndY=-57.6 EndZ=0
    g63: Circle [constr] CenterX=-14 CenterY=-73.8 CenterZ=0 NormalX=-1e-16 NormalY=0 NormalZ=1 AngleXU=-1.5708 Radius=1.1
    g64: LineSegment [constr] StartX=-14.8 StartY=-64.1 StartZ=0 EndX=-16.4 EndY=-64.1 EndZ=0
    g65: LineSegment [constr] StartX=-14.8 StartY=-54 StartZ=0 EndX=-14.8 EndY=-64.1 EndZ=0
    g66: LineSegment [constr] StartX=-16.4 StartY=-54 StartZ=0 EndX=-14.8 EndY=-54 EndZ=0
    g67: LineSegment [constr] StartX=-16.4 StartY=-64.1 StartZ=0 EndX=-16.4 EndY=-54 EndZ=0
    g68: LineSegment [constr] StartX=52 StartY=-56.2 StartZ=0 EndX=27.8 EndY=-56.2 EndZ=0
    g69: LineSegment [constr] StartX=52 StartY=-53.8 StartZ=0 EndX=52 EndY=-56.2 EndZ=0
    g70: LineSegment [constr] StartX=27.8 StartY=-53.8 StartZ=0 EndX=52 EndY=-53.8 EndZ=0
    g71: LineSegment [constr] StartX=27.8 StartY=-56.2 StartZ=0 EndX=27.8 EndY=-53.8 EndZ=0
    g72: Circle [constr] CenterX=112.6 CenterY=-23.3 CenterZ=0 NormalX=-1e-16 NormalY=0 NormalZ=1 AngleXU=-1.5708 Radius=1.1
    g73: Circle [constr] CenterX=25.9 CenterY=0.6 CenterZ=0 NormalX=-1e-16 NormalY=0 NormalZ=1 AngleXU=-1.5708 Radius=1.1
    g74: Circle CenterX=25.9 CenterY=0.6 CenterZ=0 NormalX=0 NormalY=0 NormalZ=1 AngleXU=0 Radius=1.2
    g75: Circle CenterX=25.9 CenterY=0.6 CenterZ=0 NormalX=0 NormalY=0 NormalZ=1 AngleXU=0 Radius=1.2
    g76: Circle CenterX=112.6 CenterY=-23.3 CenterZ=0 NormalX=0 NormalY=0 NormalZ=1 AngleXU=0 Radius=1.1
    g77: Circle CenterX=112.6 CenterY=-57.3 CenterZ=0 NormalX=0 NormalY=0 NormalZ=1 AngleXU=0 Radius=1.1
    g78: Circle CenterX=-14 CenterY=-73.8 CenterZ=0 NormalX=0 NormalY=0 NormalZ=1 AngleXU=0 Radius=1.2
  constraints (157):
    c: Coincident(g34,g35)
    c: Coincident(g35,g36)
    c: Coincident(g64,g67)
    c: Coincident(g66,g67)
    c: Coincident(g37,g38)
    c: Coincident(g36,g37)
    c: Coincident(g64,g65)
    c: Coincident(g65,g66)
    c: Coincident(g38,g39)
    c: Coincident(g39,g40)
    c: Coincident(g33,g34)
    c: Coincident(g32,g33)
    c: Coincident(g41,g42)
    c: Coincident(g40,g41)
    c: Coincident(g42,g43)
    c: Coincident(g43,g44)
    c: Coincident(g31,g32)
    c: Coincident(g44,g45)
    c: Coincident(g45,g46)
    c: Coincident(g46,g47)
    c: Coincident(g30,g31)
    c: Coincident(g47,g48)
    c: Coincident(g59,g62)
    c: Coincident(g61,g62)
    c: Coincident(g68,g71)
    c: Coincident(g70,g71)
    c: Coincident(g29,g30)
    c: Coincident(g28,g29)
    c: Coincident(g27,g28)
    c: Coincident(g26,g27)
    c: Coincident(g2,g48)
    c: Coincident(g0,g2)
    c: Coincident(g22,g23)
    c: Coincident(g23,g24)
    c: Coincident(g0,g1)
    c: Coincident(g21,g22)
    c: Coincident(g24,g25)
    c: Coincident(g25,g26)
    c: Coincident(g53,g54)
    c: Coincident(g52,g53)
    c: Coincident(g68,g69)
    c: Coincident(g69,g70)
    c: Coincident(g55,g56)
    c: Coincident(g54,g55)
    c: Coincident(g50,g51)
    c: Coincident(g51,g52)
    c: Coincident(g1,g3)
    c: Coincident(g50,g58)
    c: Coincident(g4,g5)
    c: Coincident(g3,g4)
    c: Coincident(g59,g60)
    c: Coincident(g60,g61)
    c: Coincident(g56,g57)
    c: Coincident(g57,g58)
    c: Coincident(g17,g18)
    c: Coincident(g16,g17)
    c: Coincident(g20,g21)
    c: Coincident(g19,g20)
    c: Coincident(g18,g19)
    c: Coincident(g5,g6)
    c: Coincident(g14,g15)
    c: Coincident(g15,g16)
    c: Coincident(g7,g8)
    c: Coincident(g6,g7)
    c: Coincident(g13,g14)
    c: Coincident(g12,g13)
    c: Coincident(g8,g9)
    c: Coincident(g11,g12)
    c: Coincident(g10,g11)
    c: Coincident(g9,g10)
    c: Block(g0)
    c: Block(g1)
    c: Block(g2)
    c: Block(g3)
    c: Block(g4)
    c: Block(g5)
    c: Block(g6)
    c: Block(g7)
    c: Block(g8)
    c: Block(g9)
    c: Block(g10)
    c: Block(g11)
    c: Block(g12)
    c: Block(g13)
    c: Block(g14)
    c: Block(g15)
    c: Block(g16)
    c: Block(g17)
    c: Block(g18)
    c: Block(g19)
    c: Block(g20)
    c: Block(g21)
    c: Block(g22)
    c: Block(g23)
    c: Block(g24)
    c: Block(g25)
    c: Block(g26)
    c: Block(g27)
    c: Block(g28)
    c: Block(g29)
    c: Block(g30)
    c: Block(g31)
    c: Block(g32)
    c: Block(g33)
    c: Block(g34)
    c: Block(g35)
    c: Block(g36)
    c: Block(g37)
    c: Block(g38)
    c: Block(g39)
    c: Block(g40)
    c: Block(g41)
    c: Block(g42)
    c: Block(g43)
    c: Block(g44)
    c: Block(g45)
    c: Block(g46)
    c: Block(g47)
    c: Block(g48)
    c: Block(g50)
    c: Block(g51)
    c: Block(g52)
    c: Block(g53)
    c: Block(g54)
    c: Block(g55)
    c: Block(g56)
    c: Block(g57)
    c: Block(g58)
    c: Block(g59)
    c: Block(g60)
    c: Block(g61)
    c: Block(g62)
    c: Block(g63)
    c: Block(g64)
    c: Block(g65)
    c: Block(g66)
    c: Block(g67)
    c: Block(g68)
    c: Block(g69)
    c: Block(g70)
    c: Block(g71)
    c: Block(g73)
    c: Diameter(g75) = 2.4
    c: Coincident(g75,g74)
    c: Equal(g75,g74)
    c: Coincident(g76,g72)
    c: Equal(g76,g72)
    c: Coincident(g77,g49)
    c: Equal(g77,g49)
    c: Diameter(g78) = 2.4
    c: Coincident(g78,g63)
    c: Diameter(g76) = 2.2
    c: Diameter(g77) = 2.2
    c: DistanceY(g49,g-1) = 57.3
    c: DistanceY(g72,g-1) = 23.3
    c: DistanceX(g-1,g72) = 112.6
    c: DistanceX(g-1,g49) = 112.6
FEATURE [PartDesign::Pocket] Pocket015
  BaseFeature = -> Pocket014
  Direction = (0,0,-1)
  Length = 20
  Length2 = 5
  Profile = -> Sketch033
  ReferenceAxis = -> Sketch033 [N_Axis]
  Refine = true
  SideType = 0
  Suppressed = false
  Type = 0
  Type2 = 0
FEATURE [PartDesign::Fillet] Fillet004
  Base = -> Pocket015 [Edge104,Edge99,Edge89]
  BaseFeature = -> Pocket015
  Radius = 1
  Refine = true
  SupportTransform = false
  Suppressed = false
  UseAllEdges = false
FEATURE [PartDesign::Fillet] Fillet005
  Base = -> Fillet004 [Edge159,Edge182,Edge181,Edge177,Edge167,Edge170,Edge166,Edge57]
  BaseFeature = -> Fillet004
  Radius = 0.499
  Refine = true
  SupportTransform = false
  Suppressed = false
  UseAllEdges = false
FEATURE [Sketcher::SketchObject] Sketch034
  ArcFitTolerance = 1e-06
  AttachmentOffset = pos=(0,0,-5.1) rot=(0,0,1;0rad)
  AttachmentSupport = -> [XY_Plane005]
  ExternalTypes = [0]
  FullyConstrained = true
  MakeInternals = false
  MapMode = 5
  Placement = pos=(0,0,-5.1) rot=(0,0,1;0rad)
  _ExternalGeoVersion = 0
  sketch-geometry (4):
    g0: LineSegment StartX=25.5 StartY=-52 StartZ=0 EndX=25.5 EndY=-62 EndZ=0
    g1: LineSegment StartX=25.5 StartY=-62 StartZ=0 EndX=65 EndY=-62 EndZ=0
    g2: LineSegment StartX=65 StartY=-62 StartZ=0 EndX=65 EndY=-52 EndZ=0
    g3: LineSegment StartX=65 StartY=-52 StartZ=0 EndX=25.5 EndY=-52 EndZ=0
  constraints (12):
    c: Coincident(g0,g1)
    c: Coincident(g1,g2)
    c: Coincident(g2,g3)
    c: Coincident(g3,g0)
    c: Vertical(g0)
    c: Vertical(g2)
    c: Horizontal(g1)
    c: Horizontal(g3)
    c: DistanceY(g0,g-1) = 52
    c: DistanceY(g0,g-1) = 62
    c: DistanceX(g-1,g0) = 25.5
    c: DistanceX(g-1,g2) = 65
FEATURE [Sketcher::SketchObject] Sketch035
  ArcFitTolerance = 1e-06
  AttachmentOffset = pos=(0,0,-5.9) rot=(0,0,1;0rad)
  AttachmentSupport = -> [XY_Plane005]
  ExternalTypes = [0]
  FullyConstrained = false
  MakeInternals = false
  MapMode = 5
  Placement = pos=(0,0,-5.9) rot=(0,0,1;0rad)
  _ExternalGeoVersion = 0
  expr: Constraints[142] = Sketch033.Constraints[142]
  expr: Constraints[149] = Sketch033.Constraints[149]
  sketch-geometry (83):
    g0: ArcOfCircle [constr] CenterX=45.3 CenterY=2.4 CenterZ=0 NormalX=-1e-16 NormalY=0 NormalZ=1 AngleXU=1.5708 Radius=1.5 StartAngle=0 EndAngle=1.22777
    g1: LineSegment [constr] StartX=59.4 StartY=3.9 StartZ=0 EndX=45.3 EndY=3.9 EndZ=0
    g2: LineSegment [constr] StartX=43.8874 StartY=2.9045 StartZ=0 EndX=43.8874 EndY=2.8 EndZ=0
    g3: ArcOfCircle [constr] CenterX=59.4 CenterY=2.4 CenterZ=0 NormalX=-1e-16 NormalY=0 NormalZ=1 AngleXU=3.90995e-07 Radius=1.5 StartAngle=0 EndAngle=1.5708
    g4: LineSegment [constr] StartX=60.9 StartY=-0.4 StartZ=0 EndX=60.9 EndY=2.4 EndZ=0
    g5: LineSegment [constr] StartX=76.4 StartY=-0.4 StartZ=0 EndX=60.9 EndY=-0.4 EndZ=0
    g6: ArcOfCircle [constr] CenterX=76.4 CenterY=-1.9 CenterZ=0 NormalX=-1e-16 NormalY=0 NormalZ=1 AngleXU=3.90995e-07 Radius=1.5 StartAngle=0 EndAngle=1.5708
    g7: LineSegment [constr] StartX=77.9 StartY=-6.3 StartZ=0 EndX=77.9 EndY=-1.9 EndZ=0
    g8: LineSegment [constr] StartX=96.4 StartY=-6.3 StartZ=0 EndX=77.9 EndY=-6.3 EndZ=0
    g9: ArcOfCircle [constr] CenterX=96.4 CenterY=-7.8 CenterZ=0 NormalX=-1e-16 NormalY=0 NormalZ=1 AngleXU=3.90995e-07 Radius=1.5 StartAngle=0 EndAngle=1.5708
    g10: LineSegment [constr] StartX=97.9 StartY=-59.8 StartZ=0 EndX=97.9 EndY=-7.8 EndZ=0
    g11: LineSegment [constr] StartX=97.9 StartY=-72.8 StartZ=0 EndX=97.9 EndY=-59.8 EndZ=0
    g12: ArcOfCircle [constr] CenterX=96.4 CenterY=-72.8 CenterZ=0 NormalX=-1e-16 NormalY=0 NormalZ=1 AngleXU=-1.5708 Radius=1.5 StartAngle=0 EndAngle=1.5708
    g13: LineSegment [constr] StartX=78 StartY=-74.3 StartZ=0 EndX=96.4 EndY=-74.3 EndZ=0
    g14: ArcOfCircle [constr] CenterX=78 CenterY=-72.8 CenterZ=0 NormalX=-1e-16 NormalY=0 NormalZ=1 AngleXU=-3.14159 Radius=1.5 StartAngle=0 EndAngle=1.5708
    g15: LineSegment [constr] StartX=76.5 StartY=-68.4 StartZ=0 EndX=76.5 EndY=-72.8 EndZ=0
    g16: LineSegment [constr] StartX=68.6 StartY=-68.4 StartZ=0 EndX=76.5 EndY=-68.4 EndZ=0
    g17: LineSegment [constr] StartX=68.6 StartY=-69.9 StartZ=0 EndX=68.6 EndY=-68.4 EndZ=0
    g18: LineSegment [constr] StartX=75 StartY=-69.9 StartZ=0 EndX=68.6 EndY=-69.9 EndZ=0
    g19: LineSegment [constr] StartX=75 StartY=-72.8 StartZ=0 EndX=75 EndY=-69.9 EndZ=0
    g20: ArcOfCircle [constr] CenterX=73.5 CenterY=-72.8 CenterZ=0 NormalX=-1e-16 NormalY=0 NormalZ=1 AngleXU=-1.5708 Radius=1.5 StartAngle=0 EndAngle=1.5708
    g21: LineSegment [constr] StartX=46.1 StartY=-74.3 StartZ=0 EndX=73.5 EndY=-74.3 EndZ=0
    g22: ArcOfCircle [constr] CenterX=46.1 CenterY=-72.8 CenterZ=0 NormalX=-1e-16 NormalY=0 NormalZ=1 AngleXU=-3.14159 Radius=1.5 StartAngle=0 EndAngle=1.5708
    g23: LineSegment [constr] StartX=44.6 StartY=-67.6 StartZ=0 EndX=44.6 EndY=-72.8 EndZ=0
    g24: LineSegment [constr] StartX=49.65 StartY=-67.6 StartZ=0 EndX=44.6 EndY=-67.6 EndZ=0
    g25: LineSegment [constr] StartX=49.65 StartY=-66.1 StartZ=0 EndX=49.65 EndY=-67.6 EndZ=0
    g26: LineSegment [constr] StartX=43.1 StartY=-66.1 StartZ=0 EndX=49.65 EndY=-66.1 EndZ=0
    g27: LineSegment [constr] StartX=43.1 StartY=-71.2 StartZ=0 EndX=43.1 EndY=-66.1 EndZ=0
    g28: ArcOfCircle [constr] CenterX=41.6 CenterY=-71.2 CenterZ=0 NormalX=-1e-16 NormalY=0 NormalZ=1 AngleXU=-1.5708 Radius=1.5 StartAngle=0 EndAngle=1.5708
    g29: LineSegment [constr] StartX=41.4 StartY=-72.7 StartZ=0 EndX=41.6 EndY=-72.7 EndZ=0
    g30: LineSegment [constr] StartX=24.227 StartY=-72.7043 StartZ=0 EndX=41.4 EndY=-72.7 EndZ=0
    g31: LineSegment [constr] StartX=6.18739 StartY=-75.9853 StartZ=0 EndX=24.227 EndY=-72.7043 EndZ=0
    g32: LineSegment [constr] StartX=-12.4977 StartY=-82.7894 StartZ=0 EndX=6.18739 EndY=-75.9853 EndZ=0
    g33: ArcOfCircle [constr] CenterX=-13.011 CenterY=-81.3799 CenterZ=0 NormalX=-1e-16 NormalY=0 NormalZ=1 AngleXU=-2.78726 Radius=1.5 StartAngle=0 EndAngle=1.56568
    g34: LineSegment [constr] StartX=-22.1 StartY=-61.1344 StartZ=0 EndX=-14.4178 EndY=-81.9004 EndZ=0
    g35: LineSegment [constr] StartX=-22.1 StartY=0 StartZ=0 EndX=-22.1 EndY=-61.1344 EndZ=0
    g36: LineSegment [constr] StartX=-16.4 StartY=0 StartZ=0 EndX=-22.1 EndY=0 EndZ=0
    g37: LineSegment [constr] StartX=-16.4 StartY=-10.5 StartZ=0 EndX=-16.4 EndY=0 EndZ=0
    g38: LineSegment [constr] StartX=-14.8 StartY=-10.5 StartZ=0 EndX=-16.4 EndY=-10.5 EndZ=0
    g39: LineSegment [constr] StartX=-14.8 StartY=0 StartZ=0 EndX=-14.8 EndY=-10.5 EndZ=0
    g40: LineSegment [constr] StartX=-5 StartY=0 StartZ=0 EndX=-14.8 EndY=0 EndZ=0
    g41: LineSegment [constr] StartX=-5 StartY=-4 StartZ=0 EndX=-5 EndY=0 EndZ=0
    g42: LineSegment [constr] StartX=5 StartY=-4 StartZ=0 EndX=-5 EndY=-4 EndZ=0
    g43: LineSegment [constr] StartX=5 StartY=0 StartZ=0 EndX=5 EndY=-4 EndZ=0
    g44: LineSegment [constr] StartX=9.9 StartY=0 StartZ=0 EndX=5 EndY=0 EndZ=0
    g45: LineSegment [constr] StartX=9.9 StartY=1.3 StartZ=0 EndX=9.9 EndY=0 EndZ=0
    g46: LineSegment [constr] StartX=23.7 StartY=1.3 StartZ=0 EndX=9.9 EndY=1.3 EndZ=0
    g47: ArcOfCircle [constr] CenterX=25.2 CenterY=1.3 CenterZ=0 NormalX=-1e-16 NormalY=0 NormalZ=1 AngleXU=1.5708 Radius=1.5 StartAngle=0 EndAngle=1.5708
    g48: LineSegment [constr] StartX=43.8874 StartY=2.8 StartZ=0 EndX=25.2 EndY=2.8 EndZ=0
    g49: Circle [constr] CenterX=112.6 CenterY=-57.3 CenterZ=0 NormalX=-1e-16 NormalY=0 NormalZ=1 AngleXU=-1.5708 Radius=1.1
    g50: ArcOfCircle [constr] CenterX=60.7 CenterY=-66.9 CenterZ=0 NormalX=-1e-16 NormalY=0 NormalZ=1 AngleXU=-3.14159 Radius=1.5 StartAngle=0 EndAngle=1.5708
    g51: LineSegment [constr] StartX=59.2 StartY=-66.1 StartZ=0 EndX=59.2 EndY=-66.9 EndZ=0
    g52: LineSegment [constr] StartX=51.15 StartY=-66.1 StartZ=0 EndX=59.2 EndY=-66.1 EndZ=0
    g53: LineSegment [constr] StartX=51.15 StartY=-67.6 StartZ=0 EndX=51.15 EndY=-66.1 EndZ=0
    g54: LineSegment [constr] StartX=56.7 StartY=-67.6 StartZ=0 EndX=51.15 EndY=-67.6 EndZ=0
    g55: LineSegment [constr] StartX=56.7 StartY=-69.9 StartZ=0 EndX=56.7 EndY=-67.6 EndZ=0
    g56: LineSegment [constr] StartX=67.1 StartY=-69.9 StartZ=0 EndX=56.7 EndY=-69.9 EndZ=0
    g57: LineSegment [constr] StartX=67.1 StartY=-68.4 StartZ=0 EndX=67.1 EndY=-69.9 EndZ=0
    g58: LineSegment [constr] StartX=60.7 StartY=-68.4 StartZ=0 EndX=67.1 EndY=-68.4 EndZ=0
    g59: LineSegment [constr] StartX=62.7 StartY=-60 StartZ=0 EndX=27.8 EndY=-60 EndZ=0
    g60: LineSegment [constr] StartX=62.7 StartY=-57.6 StartZ=0 EndX=62.7 EndY=-60 EndZ=0
    g61: LineSegment [constr] StartX=27.8 StartY=-57.6 StartZ=0 EndX=62.7 EndY=-57.6 EndZ=0
    g62: LineSegment [constr] StartX=27.8 StartY=-60 StartZ=0 EndX=27.8 EndY=-57.6 EndZ=0
    g63: Circle [constr] CenterX=-14 CenterY=-73.8 CenterZ=0 NormalX=-1e-16 NormalY=0 NormalZ=1 AngleXU=-1.5708 Radius=1.1
    g64: LineSegment [constr] StartX=-14.8 StartY=-64.1 StartZ=0 EndX=-16.4 EndY=-64.1 EndZ=0
    g65: LineSegment [constr] StartX=-14.8 StartY=-54 StartZ=0 EndX=-14.8 EndY=-64.1 EndZ=0
    g66: LineSegment [constr] StartX=-16.4 StartY=-54 StartZ=0 EndX=-14.8 EndY=-54 EndZ=0
    g67: LineSegment [constr] StartX=-16.4 StartY=-64.1 StartZ=0 EndX=-16.4 EndY=-54 EndZ=0
    g68: LineSegment [constr] StartX=52 StartY=-56.2 StartZ=0 EndX=27.8 EndY=-56.2 EndZ=0
    g69: LineSegment [constr] StartX=52 StartY=-53.8 StartZ=0 EndX=52 EndY=-56.2 EndZ=0
    g70: LineSegment [constr] StartX=27.8 StartY=-53.8 StartZ=0 EndX=52 EndY=-53.8 EndZ=0
    g71: LineSegment [constr] StartX=27.8 StartY=-56.2 StartZ=0 EndX=27.8 EndY=-53.8 EndZ=0
    g72: Circle [constr] CenterX=112.6 CenterY=-23.3 CenterZ=0 NormalX=-1e-16 NormalY=0 NormalZ=1 AngleXU=-1.5708 Radius=1.1
    g73: Circle [constr] CenterX=25.9 CenterY=0.6 CenterZ=0 NormalX=-1e-16 NormalY=0 NormalZ=1 AngleXU=-1.5708 Radius=1.1
    g74: Circle [constr] CenterX=25.9 CenterY=0.6 CenterZ=0 NormalX=0 NormalY=0 NormalZ=1 AngleXU=0 Radius=1.2
    g75: Circle [constr] CenterX=25.9 CenterY=0.6 CenterZ=0 NormalX=0 NormalY=0 NormalZ=1 AngleXU=0 Radius=1.2
    g76: Circle [constr] CenterX=112.6 CenterY=-23.3 CenterZ=0 NormalX=0 NormalY=0 NormalZ=1 AngleXU=0 Radius=1.1
    g77: Circle [constr] CenterX=112.6 CenterY=-57.3 CenterZ=0 NormalX=0 NormalY=0 NormalZ=1 AngleXU=0 Radius=1.1
    g78: Circle [constr] CenterX=-14 CenterY=-73.8 CenterZ=0 NormalX=0 NormalY=0 NormalZ=1 AngleXU=0 Radius=1.2
    g79: Circle CenterX=112.6 CenterY=-23.3 CenterZ=0 NormalX=0 NormalY=0 NormalZ=1 AngleXU=0 Radius=2.5
    g80: Circle CenterX=112.6 CenterY=-57.3 CenterZ=0 NormalX=0 NormalY=0 NormalZ=1 AngleXU=0 Radius=2.5
    g81: Circle CenterX=-14 CenterY=-73.8 CenterZ=0 NormalX=0 NormalY=0 NormalZ=1 AngleXU=0 Radius=2.5
    g82: Circle CenterX=25.9 CenterY=0.6 CenterZ=0 NormalX=0 NormalY=0 NormalZ=1 AngleXU=0 Radius=2.5
  constraints (163):
    c: Coincident(g34,g35)
    c: Coincident(g35,g36)
    c: Coincident(g64,g67)
    c: Coincident(g66,g67)
    c: Coincident(g37,g38)
    c: Coincident(g36,g37)
    c: Coincident(g64,g65)
    c: Coincident(g65,g66)
    c: Coincident(g38,g39)
    c: Coincident(g39,g40)
    c: Coincident(g33,g34)
    c: Coincident(g32,g33)
    c: Coincident(g41,g42)
    c: Coincident(g40,g41)
    c: Coincident(g42,g43)
    c: Coincident(g43,g44)
    c: Coincident(g31,g32)
    c: Coincident(g44,g45)
    c: Coincident(g45,g46)
    c: Coincident(g46,g47)
    c: Coincident(g30,g31)
    c: Coincident(g47,g48)
    c: Coincident(g59,g62)
    c: Coincident(g61,g62)
    c: Coincident(g68,g71)
    c: Coincident(g70,g71)
    c: Coincident(g29,g30)
    c: Coincident(g28,g29)
    c: Coincident(g27,g28)
    c: Coincident(g26,g27)
    c: Coincident(g2,g48)
    c: Coincident(g0,g2)
    c: Coincident(g22,g23)
    c: Coincident(g23,g24)
    c: Coincident(g0,g1)
    c: Coincident(g21,g22)
    c: Coincident(g24,g25)
    c: Coincident(g25,g26)
    c: Coincident(g53,g54)
    c: Coincident(g52,g53)
    c: Coincident(g68,g69)
    c: Coincident(g69,g70)
    c: Coincident(g55,g56)
    c: Coincident(g54,g55)
    c: Coincident(g50,g51)
    c: Coincident(g51,g52)
    c: Coincident(g1,g3)
    c: Coincident(g50,g58)
    c: Coincident(g4,g5)
    c: Coincident(g3,g4)
    c: Coincident(g59,g60)
    c: Coincident(g60,g61)
    c: Coincident(g56,g57)
    c: Coincident(g57,g58)
    c: Coincident(g17,g18)
    c: Coincident(g16,g17)
    c: Coincident(g20,g21)
    c: Coincident(g19,g20)
    c: Coincident(g18,g19)
    c: Coincident(g5,g6)
    c: Coincident(g14,g15)
    c: Coincident(g15,g16)
    c: Coincident(g7,g8)
    c: Coincident(g6,g7)
    c: Coincident(g13,g14)
    c: Coincident(g12,g13)
    c: Coincident(g8,g9)
    c: Coincident(g11,g12)
    c: Coincident(g10,g11)
    c: Coincident(g9,g10)
    c: Block(g0)
    c: Block(g1)
    c: Block(g2)
    c: Block(g3)
    c: Block(g4)
    c: Block(g5)
    c: Block(g6)
    c: Block(g7)
    c: Block(g8)
    c: Block(g9)
    c: Block(g10)
    c: Block(g11)
    c: Block(g12)
    c: Block(g13)
    c: Block(g14)
    c: Block(g15)
    c: Block(g16)
    c: Block(g17)
    c: Block(g18)
    c: Block(g19)
    c: Block(g20)
    c: Block(g21)
    c: Block(g22)
    c: Block(g23)
    c: Block(g24)
    c: Block(g25)
    c: Block(g26)
    c: Block(g27)
    c: Block(g28)
    c: Block(g29)
    c: Block(g30)
    c: Block(g31)
    c: Block(g32)
    c: Block(g33)
    c: Block(g34)
    c: Block(g35)
    c: Block(g36)
    c: Block(g37)
    c: Block(g38)
    c: Block(g39)
    c: Block(g40)
    c: Block(g41)
    c: Block(g42)
    c: Block(g43)
    c: Block(g44)
    c: Block(g45)
    c: Block(g46)
    c: Block(g47)
    c: Block(g48)
    c: Block(g50)
    c: Block(g51)
    c: Block(g52)
    c: Block(g53)
    c: Block(g54)
    c: Block(g55)
    c: Block(g56)
    c: Block(g57)
    c: Block(g58)
    c: Block(g59)
    c: Block(g60)
    c: Block(g61)
    c: Block(g62)
    c: Block(g63)
    c: Block(g64)
    c: Block(g65)
    c: Block(g66)
    c: Block(g67)
    c: Block(g68)
    c: Block(g69)
    c: Block(g70)
    c: Block(g71)
    c: Block(g73)
    c: Diameter(g75) = 2.4
    c: Coincident(g75,g74)
    c: Equal(g75,g74)
    c: Coincident(g76,g72)
    c: Equal(g76,g72)
    c: Coincident(g77,g49)
    c: Equal(g77,g49)
    c: Diameter(g78) = 2.4
    c: Coincident(g78,g63)
    c: Diameter(g79) = 5
    c: Coincident(g79,g72)
    c: Diameter(g80) = 5
    c: Coincident(g80,g49)
    c: Diameter(g81) = 5
    c: Coincident(g81,g63)
    c: Diameter(g82) = 5
    c: Coincident(g82,g73)
    c: DistanceX(g-1,g72) = 112.6
    c: DistanceX(g-1,g49) = 112.6
    c: DistanceY(g72,g-1) = 23.3
    c: DistanceY(g49,g-1) = 57.3
FEATURE [PartDesign::Pocket] Pocket017
  BaseFeature = -> Fillet005
  Direction = (0,0,-1)
  Length = 5
  Length2 = 5
  Profile = -> Sketch035
  ReferenceAxis = -> Sketch035 [N_Axis]
  Refine = true
  SideType = 0
  Suppressed = false
  Type = 0
  Type2 = 0
FEATURE [PartDesign::Pocket] Pocket016
  BaseFeature = -> Pocket017
  Direction = (0,0,-1)
  Length = 0.5
  Length2 = 5
  Profile = -> Sketch034
  ReferenceAxis = -> Sketch034 [N_Axis]
  Refine = true
  SideType = 0
  Suppressed = false
  Type = 0
  Type2 = 0
FEATURE [Sketcher::SketchObject] Sketch036
  ArcFitTolerance = 1e-06
  AttachmentOffset = pos=(0,0,-3.9) rot=(0,0,1;0rad)
  AttachmentSupport = -> [XY_Plane005]
  ExternalTypes = [0]
  FullyConstrained = false
  MakeInternals = false
  MapMode = 5
  Placement = pos=(0,0,-3.9) rot=(0,0,1;0rad)
  _ExternalGeoVersion = 0
  sketch-geometry (12):
    g0: LineSegment [constr] StartX=25 StartY=-61.158 StartZ=0 EndX=25 EndY=-92.8827 EndZ=0
    g1: LineSegment [constr] StartX=25 StartY=-92.8827 StartZ=0 EndX=76 EndY=-92.8827 EndZ=0
    g2: LineSegment [constr] StartX=76 StartY=-92.8827 StartZ=0 EndX=76 EndY=-74.6 EndZ=0
    g3: LineSegment [constr] StartX=76 StartY=-74.6 StartZ=0 EndX=81.7754 EndY=-74.6 EndZ=0
    g4: LineSegment [constr] StartX=81.7754 StartY=-74.6 StartZ=0 EndX=81.7754 EndY=-61.158 EndZ=0
    g5: LineSegment [constr] StartX=81.7754 StartY=-61.158 StartZ=0 EndX=25 EndY=-61.158 EndZ=0
    g6: LineSegment StartX=25 StartY=-61.158 StartZ=0 EndX=25 EndY=-86.4525 EndZ=0
    g7: LineSegment StartX=25 StartY=-86.4525 StartZ=0 EndX=59.3 EndY=-86.4525 EndZ=0
    g8: LineSegment StartX=59.3 StartY=-86.4525 StartZ=0 EndX=59.3 EndY=-68.7 EndZ=0
    g9: LineSegment StartX=59.3 StartY=-68.7 StartZ=0 EndX=63.7 EndY=-68.7 EndZ=0
    g10: LineSegment StartX=63.7 StartY=-68.7 StartZ=0 EndX=63.7 EndY=-61.158 EndZ=0
    g11: LineSegment StartX=63.7 StartY=-61.158 StartZ=0 EndX=25 EndY=-61.158 EndZ=0
  constraints (31):
    c: Vertical(g0)
    c: Coincident(g0,g1)
    c: Horizontal(g1)
    c: Coincident(g1,g2)
    c: Vertical(g2)
    c: Coincident(g2,g3)
    c: Horizontal(g3)
    c: Coincident(g3,g4)
    c: Vertical(g4)
    c: Coincident(g4,g5)
    c: Coincident(g5,g0)
    c: Horizontal(g5)
    c: DistanceY(g3,g-1) = 74.6
    c: DistanceX(g-1,g1) = 76
    c: DistanceX(g-1,g0) = 25
    c: Coincident(g0,g6)
    c: PointOnObject(g6,g0)
    c: Coincident(g6,g7)
    c: Horizontal(g7)
    c: Coincident(g7,g8)
    c: Vertical(g8)
    c: Coincident(g8,g9)
    c: Horizontal(g9)
    c: Coincident(g9,g10)
    c: PointOnObject(g10,g5)
    c: Vertical(g10)
    c: Coincident(g10,g11)
    c: Coincident(g11,g6)
    c: DistanceX(g-1,g10) = 63.7
    c: DistanceY(g9,g-1) = 68.7
    c: DistanceX(g-1,g8) = 59.3
FEATURE [PartDesign::Pocket] Pocket018
  BaseFeature = -> Pocket016
  Direction = (0,0,-1)
  Length = 10
  Length2 = 5
  Profile = -> Sketch036
  ReferenceAxis = -> Sketch036 [N_Axis]
  Refine = true
  Reversed = true
  SideType = 0
  Suppressed = false
  Type = 0
  Type2 = 0
FEATURE [PartDesign::Fillet] Fillet006
  Base = -> Pocket018 [Edge80,Edge82]
  BaseFeature = -> Pocket018
  Radius = 2
  Refine = true
  SupportTransform = false
  Suppressed = false
  UseAllEdges = false
FEATURE [PartDesign::Fillet] Fillet007
  Base = -> Fillet006 [Edge116,Edge134]
  BaseFeature = -> Fillet006
  Radius = 0.5
  Refine = true
  SupportTransform = false
  Suppressed = false
  UseAllEdges = false
FEATURE [Sketcher::SketchObject] Sketch038
  ArcFitTolerance = 1e-06
  AttachmentOffset = pos=(0,0,-5.1) rot=(0,0,1;0rad)
  AttachmentSupport = -> [XY_Plane005]
  ExternalTypes = [0]
  FullyConstrained = true
  MakeInternals = false
  MapMode = 5
  Placement = pos=(0,0,-5.1) rot=(0,0,1;0rad)
  _ExternalGeoVersion = 0
  sketch-geometry (5):
    g0: LineSegment [constr] StartX=-8.14984 StartY=-81.2146 StartZ=0 EndX=-10.9689 EndY=-82.2406 EndZ=0
    g1: LineSegment StartX=-10.9689 StartY=-82.2406 StartZ=0 EndX=-10.3191 EndY=-84.0261 EndZ=0
    g2: LineSegment StartX=-10.3191 StartY=-84.0261 StartZ=0 EndX=-7.5 EndY=-83 EndZ=0
    g3: LineSegment StartX=-7.5 StartY=-83 StartZ=0 EndX=-8.14984 EndY=-81.2146 EndZ=0
    g4: ArcOfCircle CenterX=-9.55938 CenterY=-81.7276 CenterZ=0 NormalX=0 NormalY=0 NormalZ=1 AngleXU=0 Radius=1.5 StartAngle=0.349066 EndAngle=3.49066
  constraints (15):
    c: Coincident(g0,g1)
    c: Coincident(g1,g2)
    c: Coincident(g2,g3)
    c: Coincident(g3,g0)
    c: DistanceX(g2,g-1) = 7.5
    c: DistanceY(g2,g-1) = 83
    c: Perpendicular(g1,g2)
    c: Perpendicular(g0,g1)
    c: Perpendicular(g3,g0)
    c: Angle(g-1,g2) = 0.349066
    c: Distance(g3,g3) = 1.9
    c: Distance(g2,g2) = 3
    c: Coincident(g4,g0)
    c: PointOnObject(g4,g0)
    c: Coincident(g4,g0)
FEATURE [PartDesign::Pocket] Pocket020
  BaseFeature = -> Fillet007
  Direction = (0,0,-1)
  Length = 2.4
  Length2 = 5
  Profile = -> Sketch038
  ReferenceAxis = -> Sketch038 [N_Axis]
  Refine = true
  Reversed = true
  SideType = 1
  Suppressed = false
  Type = 0
  Type2 = 0
FEATURE [PartDesign::Fillet] Fillet010
  Base = -> Pocket020 [Edge49,Edge51]
  BaseFeature = -> Pocket020
  Radius = 1
  Refine = true
  SupportTransform = false
  Suppressed = false
  UseAllEdges = false
FEATURE [PartDesign::Fillet] Fillet008
  Base = -> Fillet010 [Face52,Face6,Face2,Edge75,Edge76,Edge77]
  BaseFeature = -> Fillet010
  Radius = 0.3
  Refine = true
  SupportTransform = false
  Suppressed = false
  UseAllEdges = false
FEATURE [PartDesign::Body] Body002  label="case-trackball"
  AllowCompound = false
  Group = -> [Sketch028,Sketch030,Sketch029,Pad011,Sketch031,Pocket013,Sketch032,Pocket014,Sketch033,Pocket015,Sketch034,Fillet004,Fillet005,Sketch035,Pocket017,Pocket016,Sketch036,Pocket018,Fillet006,Fillet007,Sketch038,Pocket020,Fillet010,Fillet008]
  Origin = -> Origin005
  Tip = -> Fillet008
COMPONENT P4 — geometry summary ("torabo-tsuki-lp-XS-left 1"; no construction recipe available for this part):
  bounding box: 135.2 x 86.8 x 1.6 mm
  tessellated surface: 2,540 triangles
  volume: 5098 mm^3 (27% of its bounding box)
PROVENANCE & LICENSES
A FreeCAD (.FCStd) document from a public repository crawl; recipes are the document's own serialized feature recipes (and, for linked parts, companion documents' recipes).
License: other.
